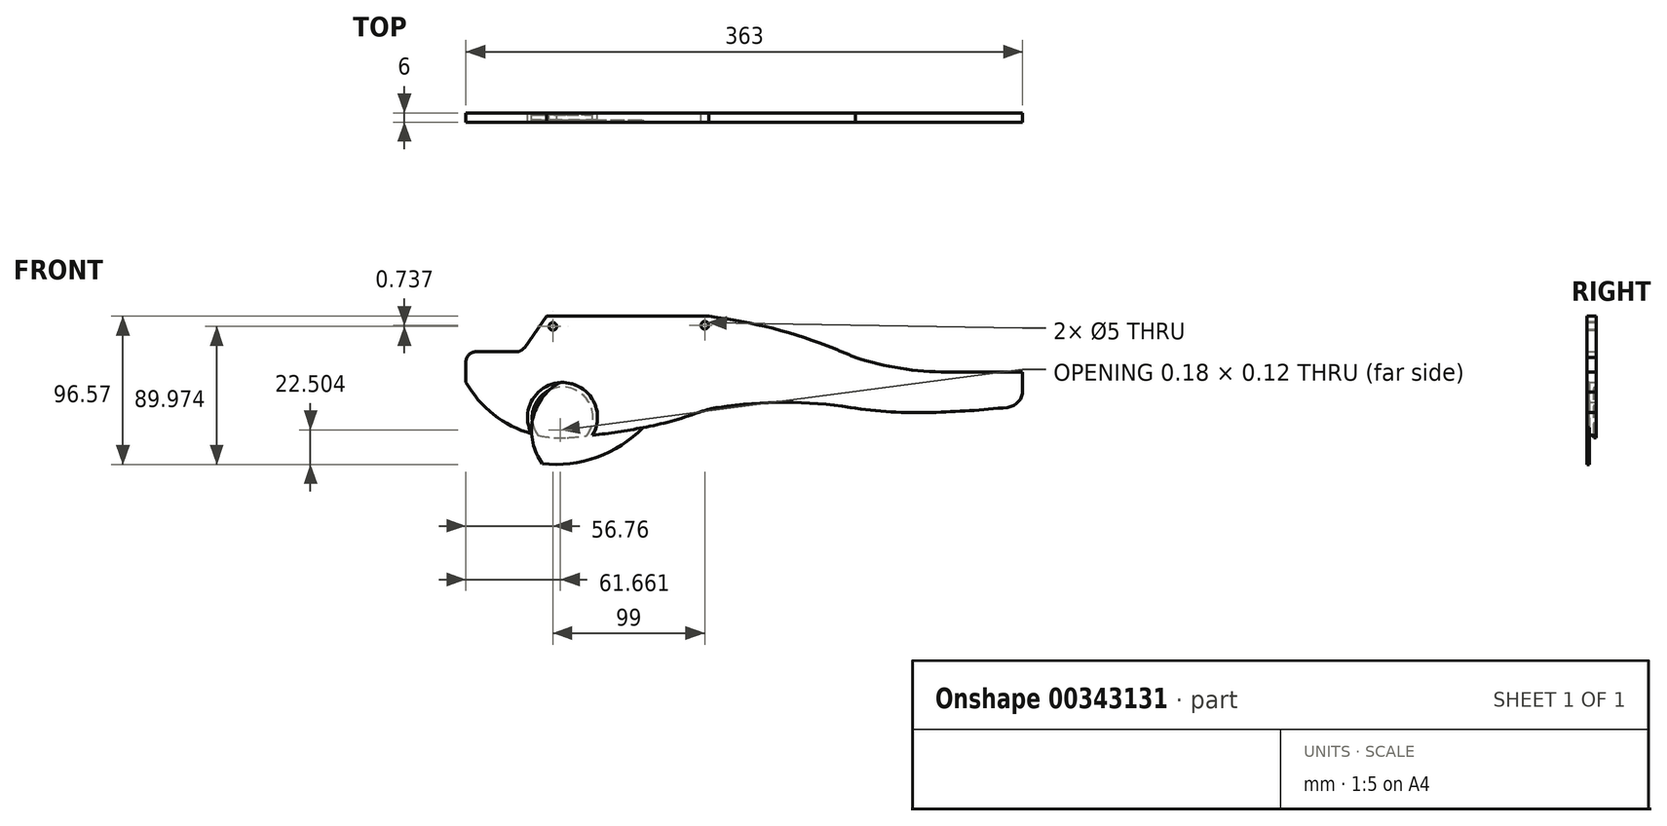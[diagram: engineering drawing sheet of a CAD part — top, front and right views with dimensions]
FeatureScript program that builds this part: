
annotation { "Feature Type Name" : "Feature", "Feature Type Description" : "" }
export const myFeature = defineFeature(function(context is Context, id is Id, definition is map)
    precondition{}
    {
        {
            var Q0;
            Q0=qCreatedBy(makeId("Front.planeOp"),FACE);
            var sketch = newSketch(context, id + "F0", { "sketchPlane" : qUnion([Q0])});
            skLineSegment(sketch, "E0", {"start": v(-42.98, -94.11) * mm, "end": v(-42.93, -88.83) * mm});
            skLineSegment(sketch, "E1", {"start": v(-26.54, -87.6) * mm, "end": v(-25.94, -92.84) * mm});
            skLineSegment(sketch, "E2", {"start": v(-57.63, -92.47) * mm, "end": v(-56.84, -87.23) * mm});
            skLineSegment(sketch, "E3", {"start": v(-60.27, -85.91) * mm, "end": v(-60.27, -101.9) * mm});
            skLineSegment(sketch, "E4", {"start": v(0.29, -136.52) * mm, "end": v(0.29, -27.62) * mm});
            skArc(sketch, "E5", {"start": v(15.17, -136.52) * mm, "mid": v(16.66, -98.58) * mm, "end": v(17.15, -60.62) * mm});
            skLineSegment(sketch, "E6", {"start": v(-95.1, -89.53) * mm, "end": v(-95.1, -113.28) * mm});
            skLineSegment(sketch, "E7", {"start": v(-82.32, -86.89) * mm, "end": v(-82.32, -118.56) * mm});
            skArc(sketch, "E8", {"start": v(-88.17, -97.12) * mm, "mid": v(-95.1, -90.19) * mm, "end": v(-102.03, -97.12) * mm});
            skLineSegment(sketch, "E9", {"start": v(-265.33, -143.12) * mm, "end": v(-265.33, 144.31) * mm});
            skLineSegment(sketch, "E10", {"start": v(173.57, -106.96) * mm, "end": v(173.57, -67.22) * mm});
            skLineSegment(sketch, "E11", {"start": v(181.5, -27.62) * mm, "end": v(181.5, -120.02) * mm});
            skLineSegment(sketch, "E12", {"start": v(-9.14, -134.54) * mm, "end": v(-9.14, -29.6) * mm});
            skLineSegment(sketch, "E13", {"start": v(-256.42, -27.62) * mm, "end": v(-256.42, -136.52) * mm});
            skLineSegment(sketch, "E14", {"start": v(-254.44, -27.62) * mm, "end": v(-254.44, -136.52) * mm});
            skLineSegment(sketch, "E15", {"start": v(9.56, -27.62) * mm, "end": v(9.56, -136.52) * mm});
            skLineSegment(sketch, "E16", {"start": v(7.58, -27.62) * mm, "end": v(7.58, -136.52) * mm});
            skLineSegment(sketch, "E17", {"start": v(-123.43, -141.8) * mm, "end": v(-123.43, -22.34) * mm});
            skCircle(sketch, "E18", {"center": v(64.91, -93.78) * mm, "radius": 4.62 * mm});
            skLineSegment(sketch, "E19", {"start": v(-115.5, -136.52) * mm, "end": v(-115.5, -27.62) * mm});
            skLineSegment(sketch, "E20", {"start": v(-113.53, -27.62) * mm, "end": v(-113.53, -136.52) * mm});
            skLineSegment(sketch, "E21", {"start": v(-131.35, -136.52) * mm, "end": v(-131.35, -27.62) * mm});
            skLineSegment(sketch, "E22", {"start": v(-133.33, -27.62) * mm, "end": v(-133.33, -136.52) * mm});
            skLineSegment(sketch, "E23", {"start": v(8.57, -27.62) * mm, "end": v(8.57, -136.52) * mm});
            skLineSegment(sketch, "E24", {"start": v(-255.43, -136.52) * mm, "end": v(-255.43, -27.62) * mm});
            skLineSegment(sketch, "E25", {"start": v(-141.07, -96.5) * mm, "end": v(-141.07, -91.3) * mm});
            skLineSegment(sketch, "E26", {"start": v(-246.67, -96.5) * mm, "end": v(-246.67, -91.3) * mm});
            skLineSegment(sketch, "E27", {"start": v(15.17, -27.62) * mm, "end": v(15.17, -136.52) * mm});
            skLineSegment(sketch, "E28", {"start": v(282.47, 144.31) * mm, "end": v(282.47, -143.12) * mm});
            skLineSegment(sketch, "E29", {"start": v(-47.86, -100.58) * mm, "end": v(-62.91, -100.58) * mm});
            skLineSegment(sketch, "E30", {"start": v(-255.43, -134.54) * mm, "end": v(8.57, -134.54) * mm});
            skLineSegment(sketch, "E31", {"start": v(-255.43, -136.52) * mm, "end": v(8.57, -136.52) * mm});
            skLineSegment(sketch, "E32", {"start": v(-265.33, -143.12) * mm, "end": v(282.47, -143.12) * mm});
            skCircle(sketch, "E33", {"center": v(-165.87, -104.46) * mm, "radius": 4.62 * mm});
            skLineSegment(sketch, "E34", {"start": v(-246.67, -97.09) * mm, "end": v(-141.07, -97.09) * mm});
            skLineSegment(sketch, "E35", {"start": v(-141.07, -112.93) * mm, "end": v(-246.67, -112.93) * mm});
            skLineSegment(sketch, "E36", {"start": v(-242, -92.47) * mm, "end": v(-141.07, -92.47) * mm});
            skLineSegment(sketch, "E37", {"start": v(-256.42, -136.52) * mm, "end": v(-255.43, -136.52) * mm});
            skLineSegment(sketch, "E38", {"start": v(-246.67, -112.93) * mm, "end": v(-246.67, -97.09) * mm});
            skLineSegment(sketch, "E39", {"start": v(-236.7, -112.93) * mm, "end": v(-240.57, -112.93) * mm});
            skLineSegment(sketch, "E40", {"start": v(-239.4, -108.26) * mm, "end": v(-239.4, -101.75) * mm});
            skLineSegment(sketch, "E41", {"start": v(-236.7, -97.09) * mm, "end": v(-240.57, -97.09) * mm});
            skLineSegment(sketch, "E42", {"start": v(-143.23, -133.22) * mm, "end": v(-103.63, -133.22) * mm});
            skLineSegment(sketch, "E43", {"start": v(-143.23, -136.52) * mm, "end": v(-143.23, -133.22) * mm});
            skLineSegment(sketch, "E44", {"start": v(-130.03, -143.12) * mm, "end": v(-130.03, -146.42) * mm});
            skLineSegment(sketch, "E45", {"start": v(-141.07, -112.93) * mm, "end": v(-141.07, -97.09) * mm});
            skLineSegment(sketch, "E46", {"start": v(-148.76, -103.08) * mm, "end": v(-156.68, -103.08) * mm});
            skLineSegment(sketch, "E47", {"start": v(-156.68, -103.08) * mm, "end": v(-154.52, -102.08) * mm});
            skLineSegment(sketch, "E48", {"start": v(-148.76, -103.08) * mm, "end": v(-150.91, -104.08) * mm});
            skLineSegment(sketch, "E49", {"start": v(-103.63, -133.22) * mm, "end": v(-103.63, -136.52) * mm});
            skLineSegment(sketch, "E50", {"start": v(-79.02, -103.38) * mm, "end": v(-85.62, -103.38) * mm});
            skLineSegment(sketch, "E51", {"start": v(-79.02, -113.28) * mm, "end": v(-85.62, -113.28) * mm});
            skArc(sketch, "E52", {"start": v(-91.47, -113.28) * mm, "mid": v(-89, -105.37) * mm, "end": v(-88.17, -97.12) * mm});
            skArc(sketch, "E53", {"start": v(-102.03, -97.12) * mm, "mid": v(-101.2, -105.37) * mm, "end": v(-98.73, -113.28) * mm});
            skLineSegment(sketch, "E54", {"start": v(-98.07, -103.38) * mm, "end": v(-98.07, -113.28) * mm});
            skLineSegment(sketch, "E55", {"start": v(-92.13, -103.38) * mm, "end": v(-92.13, -113.28) * mm});
            skLineSegment(sketch, "E56", {"start": v(-98.07, -113.28) * mm, "end": v(-98.73, -113.28) * mm});
            skLineSegment(sketch, "E57", {"start": v(-86.85, -118.56) * mm, "end": v(-103.35, -118.56) * mm});
            skLineSegment(sketch, "E58", {"start": v(-92.13, -113.28) * mm, "end": v(-91.47, -113.28) * mm});
            skLineSegment(sketch, "E59", {"start": v(-98.07, -115.26) * mm, "end": v(-98.07, -121.86) * mm});
            skLineSegment(sketch, "E60", {"start": v(-92.13, -115.26) * mm, "end": v(-92.13, -121.86) * mm});
            skLineSegment(sketch, "E61", {"start": v(-99.37, -94.25) * mm, "end": v(-97.97, -92.85) * mm});
            skCircle(sketch, "E62", {"center": v(-98.67, -93.55) * mm, "radius": 0.66 * mm});
            skLineSegment(sketch, "E63", {"start": v(-99.37, -92.85) * mm, "end": v(-97.97, -94.25) * mm});
            skLineSegment(sketch, "E64", {"start": v(-99.37, -99.99) * mm, "end": v(-97.97, -101.39) * mm});
            skCircle(sketch, "E65", {"center": v(-98.67, -100.69) * mm, "radius": 0.66 * mm});
            skLineSegment(sketch, "E66", {"start": v(-99.37, -101.39) * mm, "end": v(-97.97, -99.99) * mm});
            skLineSegment(sketch, "E67", {"start": v(-102.69, -97.12) * mm, "end": v(-87.5, -97.12) * mm});
            skLineSegment(sketch, "E68", {"start": v(-92.23, -92.85) * mm, "end": v(-90.83, -94.25) * mm});
            skCircle(sketch, "E69", {"center": v(-91.53, -93.55) * mm, "radius": 0.66 * mm});
            skLineSegment(sketch, "E70", {"start": v(-92.23, -94.25) * mm, "end": v(-90.83, -92.85) * mm});
            skLineSegment(sketch, "E71", {"start": v(-92.13, -103.38) * mm, "end": v(-98.07, -103.38) * mm});
            skCircle(sketch, "E72", {"center": v(-91.53, -100.69) * mm, "radius": 0.66 * mm});
            skLineSegment(sketch, "E73", {"start": v(-92.23, -101.39) * mm, "end": v(-90.83, -99.99) * mm});
            skLineSegment(sketch, "E74", {"start": v(-92.23, -99.99) * mm, "end": v(-90.83, -101.39) * mm});
            skCircle(sketch, "E75", {"center": v(-95.1, -97.12) * mm, "radius": 1.98 * mm});
            skCircle(sketch, "E76", {"center": v(-73.58, -113.75) * mm, "radius": 4.62 * mm});
            skLineSegment(sketch, "E77", {"start": v(15.17, -136.52) * mm, "end": v(162.34, -120.02) * mm});
            skArc(sketch, "E78", {"start": v(-57.63, -92.47) * mm, "mid": v(-41.88, -100.58) * mm, "end": v(-25.94, -92.84) * mm});
            skArc(sketch, "E79", {"start": v(-47.27, -93.95) * mm, "mid": v(-45.12, -94.06) * mm, "end": v(-42.98, -94.11) * mm});
            skArc(sketch, "E80", {"start": v(-46.25, -100.04) * mm, "mid": v(-44.67, -99.16) * mm, "end": v(-45.46, -97.53) * mm});
            skArc(sketch, "E81", {"start": v(-47.25, -93.95) * mm, "mid": v(-48.63, -94.95) * mm, "end": v(-47.86, -96.48) * mm});
            skLineSegment(sketch, "E82", {"start": v(-47.86, -96.48) * mm, "end": v(-45.42, -97.55) * mm});
            skLineSegment(sketch, "E83", {"start": v(8.57, -143.12) * mm, "end": v(8.57, -146.42) * mm});
            skLineSegment(sketch, "E84", {"start": v(9.56, -136.52) * mm, "end": v(8.57, -136.52) * mm});
            skLineSegment(sketch, "E85", {"start": v(72.28, -137.45) * mm, "end": v(138.28, -137.45) * mm});
            skLineSegment(sketch, "E86", {"start": v(72.28, -138.77) * mm, "end": v(138.28, -138.77) * mm});
            skLineSegment(sketch, "E87", {"start": v(72.28, -138.11) * mm, "end": v(138.28, -138.11) * mm});
            skLineSegment(sketch, "E88", {"start": v(72.28, -137.45) * mm, "end": v(72.28, -135.8) * mm});
            skLineSegment(sketch, "E89", {"start": v(72.28, -138.77) * mm, "end": v(72.28, -137.45) * mm});
            skLineSegment(sketch, "E90", {"start": v(75.58, -138.77) * mm, "end": v(75.58, -137.45) * mm});
            skLineSegment(sketch, "E91", {"start": v(74.92, -138.77) * mm, "end": v(74.92, -137.45) * mm});
            skLineSegment(sketch, "E92", {"start": v(74.26, -138.77) * mm, "end": v(74.26, -137.45) * mm});
            skLineSegment(sketch, "E93", {"start": v(73.6, -138.77) * mm, "end": v(73.6, -137.45) * mm});
            skLineSegment(sketch, "E94", {"start": v(72.94, -138.77) * mm, "end": v(72.94, -137.45) * mm});
            skLineSegment(sketch, "E95", {"start": v(78.88, -138.77) * mm, "end": v(78.88, -135.8) * mm});
            skLineSegment(sketch, "E96", {"start": v(78.22, -138.77) * mm, "end": v(78.22, -137.45) * mm});
            skLineSegment(sketch, "E97", {"start": v(85.48, -138.77) * mm, "end": v(85.48, -135.8) * mm});
            skLineSegment(sketch, "E98", {"start": v(77.56, -138.77) * mm, "end": v(77.56, -137.45) * mm});
            skLineSegment(sketch, "E99", {"start": v(76.9, -138.77) * mm, "end": v(76.9, -137.45) * mm});
            skLineSegment(sketch, "E100", {"start": v(76.24, -138.77) * mm, "end": v(76.24, -137.45) * mm});
            skLineSegment(sketch, "E101", {"start": v(98.68, -138.77) * mm, "end": v(98.68, -135.8) * mm});
            skLineSegment(sketch, "E102", {"start": v(92.08, -138.77) * mm, "end": v(92.08, -135.8) * mm});
            skLineSegment(sketch, "E103", {"start": v(61.37, -106.33) * mm, "end": v(63.52, -105.33) * mm});
            skLineSegment(sketch, "E104", {"start": v(69.29, -106.33) * mm, "end": v(61.37, -106.33) * mm});
            skLineSegment(sketch, "E105", {"start": v(69.29, -106.33) * mm, "end": v(67.13, -107.34) * mm});
            skLineSegment(sketch, "E106", {"start": v(111.88, -138.77) * mm, "end": v(111.88, -135.8) * mm});
            skLineSegment(sketch, "E107", {"start": v(105.28, -138.77) * mm, "end": v(105.28, -135.8) * mm});
            skLineSegment(sketch, "E108", {"start": v(118.48, -138.77) * mm, "end": v(118.48, -135.8) * mm});
            skLineSegment(sketch, "E109", {"start": v(125.08, -138.77) * mm, "end": v(125.08, -135.8) * mm});
            skLineSegment(sketch, "E110", {"start": v(147.17, -143.12) * mm, "end": v(147.17, -146.42) * mm});
            skLineSegment(sketch, "E111", {"start": v(138.28, -138.77) * mm, "end": v(138.28, -135.8) * mm});
            skLineSegment(sketch, "E112", {"start": v(131.68, -138.77) * mm, "end": v(131.68, -135.8) * mm});
            skLineSegment(sketch, "E113", {"start": v(160.37, -106.96) * mm, "end": v(169.7, -116.3) * mm});
            skArc(sketch, "E114", {"start": v(162.34, -120.02) * mm, "mid": v(170.38, -115.57) * mm, "end": v(173.57, -106.96) * mm});
            skLineSegment(sketch, "E115", {"start": v(174.9, -120.02) * mm, "end": v(181.5, -120.02) * mm});
            skLineSegment(sketch, "E116", {"start": v(160.37, -105.31) * mm, "end": v(160.37, -108.61) * mm});
            skLineSegment(sketch, "E117", {"start": v(162.02, -106.96) * mm, "end": v(158.72, -106.96) * mm});
            skLineSegment(sketch, "E118", {"start": v(-24.62, -84.06) * mm, "end": v(-58.95, -84.06) * mm});
            skLineSegment(sketch, "E119", {"start": v(-57.63, -87.23) * mm, "end": v(-62.91, -87.23) * mm});
            skLineSegment(sketch, "E120", {"start": v(124.6, 13.25) * mm, "end": v(-257.96, 13.25) * mm});
            skLineSegment(sketch, "E121", {"start": v(-54.8, 33.74) * mm, "end": v(-61.25, 33.74) * mm});
            skLineSegment(sketch, "E122", {"start": v(-54.8, 43.64) * mm, "end": v(-61.25, 43.64) * mm});
            skLineSegment(sketch, "E123", {"start": v(69.74, 85.08) * mm, "end": v(-206.13, 85.08) * mm});
            skLineSegment(sketch, "E124", {"start": v(-240.46, 57.71) * mm, "end": v(-39.87, 57.71) * mm});
            skLineSegment(sketch, "E125", {"start": v(-255.43, -29.6) * mm, "end": v(8.57, -29.6) * mm});
            skLineSegment(sketch, "E126", {"start": v(-255.43, -27.62) * mm, "end": v(8.57, -27.62) * mm});
            skArc(sketch, "E127", {"start": v(0.09, 100.16) * mm, "mid": v(-40.3, 113.45) * mm, "end": v(-82.06, 121.38) * mm});
            skLineSegment(sketch, "E128", {"start": v(-82.06, 16.22) * mm, "end": v(122.54, 16.22) * mm});
            skLineSegment(sketch, "E129", {"start": v(-82.06, 12.26) * mm, "end": v(122.54, 12.26) * mm});
            skLineSegment(sketch, "E130", {"start": v(-82.06, 10.28) * mm, "end": v(122.54, 10.28) * mm});
            skLineSegment(sketch, "E131", {"start": v(-67.32, 121.38) * mm, "end": v(11.5, 121.38) * mm});
            skLineSegment(sketch, "E132", {"start": v(122.54, 14.24) * mm, "end": v(-82.06, 14.24) * mm});
            skArc(sketch, "E133", {"start": v(10.34, 61.98) * mm, "mid": v(-32.56, 65.28) * mm, "end": v(-75.46, 61.98) * mm});
            skLineSegment(sketch, "E134", {"start": v(-265.33, 144.31) * mm, "end": v(282.47, 144.31) * mm});
            skArc(sketch, "E135", {"start": v(-178.9, 47.37) * mm, "mid": v(-178.8, 47.37) * mm, "end": v(-178.7, 47.37) * mm});
            skArc(sketch, "E136", {"start": v(-171.6, 95.7) * mm, "mid": v(-190.86, 66.6) * mm, "end": v(-165.14, 43) * mm});
            skArc(sketch, "E137", {"start": v(-240.46, 78.48) * mm, "mid": v(-223.34, 58.17) * mm, "end": v(-199.98, 45.5) * mm});
            skLineSegment(sketch, "E138", {"start": v(-240.46, 76.5) * mm, "end": v(-240.46, 31.72) * mm});
            skArc(sketch, "E139", {"start": v(-174.46, 42.18) * mm, "mid": v(-149.62, 44.8) * mm, "end": v(-124.96, 48.78) * mm});
            skArc(sketch, "E140", {"start": v(-193.4, 43.74) * mm, "mid": v(-177.66, 35.62) * mm, "end": v(-161.72, 43.36) * mm});
            skLineSegment(sketch, "E141", {"start": v(-176, -4.6) * mm, "end": v(-157.01, -4.6) * mm});
            skLineSegment(sketch, "E142", {"start": v(-161.03, 31.18) * mm, "end": v(-167.86, 22.82) * mm});
            skLineSegment(sketch, "E143", {"start": v(-174.46, 9.62) * mm, "end": v(-161.26, 9.62) * mm});
            skLineSegment(sketch, "E144", {"start": v(-174.46, 22.82) * mm, "end": v(-161.26, 22.82) * mm});
            skLineSegment(sketch, "E145", {"start": v(-167.86, 6.98) * mm, "end": v(-161.26, 6.98) * mm});
            skLineSegment(sketch, "E146", {"start": v(-166.54, 4.34) * mm, "end": v(-162.58, 4.34) * mm});
            skArc(sketch, "E147", {"start": v(-141.07, -66.86) * mm, "mid": v(-177.15, -60.34) * mm, "end": v(-213.67, -56.96) * mm});
            skLineSegment(sketch, "E148", {"start": v(-246.67, -66.86) * mm, "end": v(-141.07, -66.86) * mm});
            skArc(sketch, "E149", {"start": v(-140.63, -64.93) * mm, "mid": v(-176.88, -58.38) * mm, "end": v(-213.57, -54.98) * mm});
            skLineSegment(sketch, "E150", {"start": v(-243.79, -64.88) * mm, "end": v(-150.34, -64.88) * mm});
            skLineSegment(sketch, "E151", {"start": v(-174.46, 10.28) * mm, "end": v(-161.26, 10.28) * mm});
            skLineSegment(sketch, "E152", {"start": v(-174.46, 12.26) * mm, "end": v(-161.26, 12.26) * mm});
            skLineSegment(sketch, "E153", {"start": v(-174.46, 16.22) * mm, "end": v(-161.26, 16.22) * mm});
            skLineSegment(sketch, "E154", {"start": v(-161.26, 14.24) * mm, "end": v(-174.46, 14.24) * mm});
            skLineSegment(sketch, "E155", {"start": v(-255.43, -25.64) * mm, "end": v(-255.43, -9.14) * mm});
            skArc(sketch, "E156", {"start": v(-213.67, -56.96) * mm, "mid": v(-231.03, -59.03) * mm, "end": v(-246.67, -66.86) * mm});
            skArc(sketch, "E157", {"start": v(-213.57, -54.98) * mm, "mid": v(-231.01, -56.96) * mm, "end": v(-246.85, -64.55) * mm});
            skLineSegment(sketch, "E158", {"start": v(-244.2, -54.23) * mm, "end": v(-246.94, -65.4) * mm});
            skLineSegment(sketch, "E159", {"start": v(-246.33, -64.18) * mm, "end": v(-245.17, -65.79) * mm});
            skArc(sketch, "E160", {"start": v(-246.85, -64.55) * mm, "mid": v(-247.42, -65.75) * mm, "end": v(-246.67, -66.86) * mm});
            skLineSegment(sketch, "E161", {"start": v(-255.43, -27.62) * mm, "end": v(-256.42, -27.62) * mm});
            skLineSegment(sketch, "E162", {"start": v(-255.43, -27.62) * mm, "end": v(-254.1, -27.62) * mm});
            skLineSegment(sketch, "E163", {"start": v(-244.2, -54.23) * mm, "end": v(-238.71, -54.23) * mm});
            skLineSegment(sketch, "E164", {"start": v(-186.91, -52.29) * mm, "end": v(-188.29, -57.87) * mm});
            skLineSegment(sketch, "E165", {"start": v(-198.1, -66.02) * mm, "end": v(-186.91, -52.29) * mm});
            skLineSegment(sketch, "E166", {"start": v(-186.91, -52.29) * mm, "end": v(-170.37, -52.29) * mm});
            skLineSegment(sketch, "E167", {"start": v(-240.87, 21.06) * mm, "end": v(-194.44, 21.06) * mm});
            skLineSegment(sketch, "E168", {"start": v(-233.12, 10.28) * mm, "end": v(-187.66, 10.28) * mm});
            skLineSegment(sketch, "E169", {"start": v(-233.01, 16.22) * mm, "end": v(-187.66, 16.22) * mm});
            skLineSegment(sketch, "E170", {"start": v(-233.08, 12.26) * mm, "end": v(-187.66, 12.26) * mm});
            skLineSegment(sketch, "E171", {"start": v(-187.66, 14.24) * mm, "end": v(-233.05, 14.24) * mm});
            skLineSegment(sketch, "E172", {"start": v(-253.18, 12.9) * mm, "end": v(-253.15, 14.28) * mm});
            skLineSegment(sketch, "E173", {"start": v(-251.24, 12.85) * mm, "end": v(-251.21, 14.24) * mm});
            skLineSegment(sketch, "E174", {"start": v(-257.96, 13.66) * mm, "end": v(-219.59, 13) * mm});
            skLineSegment(sketch, "E175", {"start": v(-233.94, 19.85) * mm, "end": v(-234.17, 6.65) * mm});
            skLineSegment(sketch, "E176", {"start": v(-232.95, 19.83) * mm, "end": v(-233.18, 6.63) * mm});
            skLineSegment(sketch, "E177", {"start": v(-233.95, 19.19) * mm, "end": v(-234.16, 7.3) * mm});
            skLineSegment(sketch, "E178", {"start": v(-235.68, 7.33) * mm, "end": v(-235.47, 19.21) * mm});
            skLineSegment(sketch, "E179", {"start": v(-242.06, 8.67) * mm, "end": v(-241.9, 18.1) * mm});
            skLineSegment(sketch, "E180", {"start": v(-246.94, 8.75) * mm, "end": v(-246.78, 18.19) * mm});
            skLineSegment(sketch, "E181", {"start": v(-251.27, 10.77) * mm, "end": v(-249.63, 10.75) * mm});
            skLineSegment(sketch, "E182", {"start": v(-251.18, 16.32) * mm, "end": v(-249.53, 16.29) * mm});
            skLineSegment(sketch, "E183", {"start": v(-251.27, 10.77) * mm, "end": v(-251.18, 16.32) * mm});
            skLineSegment(sketch, "E184", {"start": v(-252.75, 12.32) * mm, "end": v(-252.7, 14.83) * mm});
            skLineSegment(sketch, "E185", {"start": v(-252.7, 14.83) * mm, "end": v(-251.2, 14.8) * mm});
            skLineSegment(sketch, "E186", {"start": v(-252.75, 12.32) * mm, "end": v(-251.25, 12.3) * mm});
            skLineSegment(sketch, "E187", {"start": v(-238.83, 10.03) * mm, "end": v(-238.72, 16.63) * mm});
            skLineSegment(sketch, "E188", {"start": v(-241.94, 15.36) * mm, "end": v(-238.74, 15.3) * mm});
            skLineSegment(sketch, "E189", {"start": v(-249.63, 10.75) * mm, "end": v(-249.53, 16.29) * mm});
            skLineSegment(sketch, "E190", {"start": v(-238.72, 16.63) * mm, "end": v(-235.52, 16.57) * mm});
            skLineSegment(sketch, "E191", {"start": v(-246.78, 18.19) * mm, "end": v(-241.9, 18.1) * mm});
            skLineSegment(sketch, "E192", {"start": v(-235.47, 19.21) * mm, "end": v(-233.95, 19.19) * mm});
            skLineSegment(sketch, "E193", {"start": v(-238.83, 10.03) * mm, "end": v(-235.63, 9.97) * mm});
            skLineSegment(sketch, "E194", {"start": v(-247.87, 12.5) * mm, "end": v(-247.83, 14.48) * mm});
            skLineSegment(sketch, "E195", {"start": v(-248.52, 12.5) * mm, "end": v(-248.5, 14.49) * mm});
            skLineSegment(sketch, "E196", {"start": v(-247.83, 14.48) * mm, "end": v(-246.84, 14.46) * mm});
            skLineSegment(sketch, "E197", {"start": v(-249.55, 14.77) * mm, "end": v(-248.5, 14.49) * mm});
            skLineSegment(sketch, "E198", {"start": v(-248.52, 13) * mm, "end": v(-247.86, 13) * mm});
            skLineSegment(sketch, "E199", {"start": v(-248.5, 14) * mm, "end": v(-247.84, 13.98) * mm});
            skLineSegment(sketch, "E200", {"start": v(-242, 11.4) * mm, "end": v(-238.8, 11.35) * mm});
            skLineSegment(sketch, "E201", {"start": v(-247.87, 12.5) * mm, "end": v(-246.88, 12.48) * mm});
            skLineSegment(sketch, "E202", {"start": v(-249.6, 12.26) * mm, "end": v(-248.52, 12.5) * mm});
            skLineSegment(sketch, "E203", {"start": v(-246.94, 8.75) * mm, "end": v(-242.06, 8.67) * mm});
            skLineSegment(sketch, "E204", {"start": v(-235.68, 7.33) * mm, "end": v(-234.16, 7.3) * mm});
            skLineSegment(sketch, "E205", {"start": v(-240.46, 16.22) * mm, "end": v(-240.46, 10.28) * mm});
            skLineSegment(sketch, "E206", {"start": v(-251.6, -1.17) * mm, "end": v(-251.24, 12.85) * mm});
            skLineSegment(sketch, "E207", {"start": v(-253.18, 12.9) * mm, "end": v(-253.19, -1.87) * mm});
            skLineSegment(sketch, "E208", {"start": v(-234.17, 6.65) * mm, "end": v(-233.18, 6.63) * mm});
            skLineSegment(sketch, "E209", {"start": v(-240.46, 10.28) * mm, "end": v(-234.1, 10.28) * mm});
            skLineSegment(sketch, "E210", {"start": v(-251.05, 33.32) * mm, "end": v(-251.22, 14.25) * mm});
            skLineSegment(sketch, "E211", {"start": v(-253.15, 14.28) * mm, "end": v(-252.49, 33.79) * mm});
            skLineSegment(sketch, "E212", {"start": v(-240.87, 21.06) * mm, "end": v(-243.25, 18.15) * mm});
            skLineSegment(sketch, "E213", {"start": v(-233.94, 19.85) * mm, "end": v(-232.95, 19.83) * mm});
            skLineSegment(sketch, "E214", {"start": v(-240.46, 16.22) * mm, "end": v(-234, 16.22) * mm});
            skLineSegment(sketch, "E215", {"start": v(-179.64, 16.76) * mm, "end": v(-179.64, 8.84) * mm});
            skLineSegment(sketch, "E216", {"start": v(-187.66, 3.35) * mm, "end": v(-187.66, 23.15) * mm});
            skLineSegment(sketch, "E217", {"start": v(-174.46, 23.15) * mm, "end": v(-174.46, 3.35) * mm});
            skLineSegment(sketch, "E218", {"start": v(-185.02, 3.35) * mm, "end": v(-185.02, 23.15) * mm});
            skLineSegment(sketch, "E219", {"start": v(-182.38, 23.15) * mm, "end": v(-182.38, 3.35) * mm});
            skLineSegment(sketch, "E220", {"start": v(-209.11, 14.24) * mm, "end": v(-209.11, 12.26) * mm});
            skLineSegment(sketch, "E221", {"start": v(-212.41, 14.24) * mm, "end": v(-212.41, 12.26) * mm});
            skCircle(sketch, "E222", {"center": v(-193.46, 4.9) * mm, "radius": 4.62 * mm});
            skLineSegment(sketch, "E223", {"start": v(-176, -4.6) * mm, "end": v(-183.7, 1.7) * mm});
            skLineSegment(sketch, "E224", {"start": v(-174.46, 3.35) * mm, "end": v(-187.66, 3.35) * mm});
            skLineSegment(sketch, "E225", {"start": v(-182.38, 3.35) * mm, "end": v(-182.38, 1.7) * mm});
            skLineSegment(sketch, "E226", {"start": v(-185.02, 3.35) * mm, "end": v(-185.02, 1.7) * mm});
            skLineSegment(sketch, "E227", {"start": v(-182.38, 1.7) * mm, "end": v(-185.02, 1.7) * mm});
            skLineSegment(sketch, "E228", {"start": v(-179.64, 8.84) * mm, "end": v(-180.64, 11) * mm});
            skLineSegment(sketch, "E229", {"start": v(-167.86, 6.98) * mm, "end": v(-167.86, 9.62) * mm});
            skLineSegment(sketch, "E230", {"start": v(-167.86, 8.3) * mm, "end": v(-169.84, 8.3) * mm});
            skLineSegment(sketch, "E231", {"start": v(-169.84, 8.3) * mm, "end": v(-169.84, 9.62) * mm});
            skLineSegment(sketch, "E232", {"start": v(-166.54, 4.34) * mm, "end": v(-166.54, 6.98) * mm});
            skArc(sketch, "E233", {"start": v(-199.98, 45.5) * mm, "mid": v(-187.37, 42.69) * mm, "end": v(-174.46, 42.18) * mm});
            skLineSegment(sketch, "E234", {"start": v(-179.64, 16.76) * mm, "end": v(-178.64, 14.61) * mm});
            skLineSegment(sketch, "E235", {"start": v(-187.66, 23.15) * mm, "end": v(-174.46, 23.15) * mm});
            skLineSegment(sketch, "E236", {"start": v(-182.38, 24.8) * mm, "end": v(-182.38, 23.15) * mm});
            skLineSegment(sketch, "E237", {"start": v(-185.02, 24.8) * mm, "end": v(-185.02, 23.15) * mm});
            skLineSegment(sketch, "E238", {"start": v(-185.02, 24.8) * mm, "end": v(-182.38, 24.8) * mm});
            skArc(sketch, "E239", {"start": v(-182.02, 36.16) * mm, "mid": v(-182, 36.16) * mm, "end": v(-182, 36.16) * mm});
            skLineSegment(sketch, "E240", {"start": v(-181.23, 38.67) * mm, "end": v(-181.2, 38.66) * mm});
            skArc(sketch, "E241", {"start": v(-183.02, 42.26) * mm, "mid": v(-183.03, 42.26) * mm, "end": v(-183.04, 42.26) * mm});
            skLineSegment(sketch, "E242", {"start": v(-178.7, 47.25) * mm, "end": v(-178.7, 47.37) * mm});
            skCircle(sketch, "E243", {"center": v(-104.66, -18.88) * mm, "radius": 4.62 * mm});
            skLineSegment(sketch, "E244", {"start": v(-97.03, -22.95) * mm, "end": v(-97.03, -18.28) * mm});
            skLineSegment(sketch, "E245", {"start": v(-133.33, -26.3) * mm, "end": v(-133.33, -19.04) * mm});
            skLineSegment(sketch, "E246", {"start": v(-113.53, -26.3) * mm, "end": v(-113.53, -19.04) * mm});
            skLineSegment(sketch, "E247", {"start": v(-138.56, -36.7) * mm, "end": v(-108.3, -36.7) * mm});
            skLineSegment(sketch, "E248", {"start": v(-143.23, -30.92) * mm, "end": v(-103.63, -30.92) * mm});
            skCircle(sketch, "E249", {"center": v(-156.91, -73.53) * mm, "radius": 4.62 * mm});
            skLineSegment(sketch, "E250", {"start": v(-160.11, -70.2) * mm, "end": v(-164.23, -65.92) * mm});
            skLineSegment(sketch, "E251", {"start": v(-140.63, -64.93) * mm, "end": v(-141.07, -66.86) * mm});
            skLineSegment(sketch, "E252", {"start": v(-142.56, -64.5) * mm, "end": v(-143, -66.43) * mm});
            skLineSegment(sketch, "E253", {"start": v(-143.26, -59.23) * mm, "end": v(-141.7, -65.6) * mm});
            skLineSegment(sketch, "E254", {"start": v(-148.95, -59.23) * mm, "end": v(-143.26, -59.23) * mm});
            skLineSegment(sketch, "E255", {"start": v(-143.23, -32.24) * mm, "end": v(-143.23, -38.69) * mm});
            skLineSegment(sketch, "E256", {"start": v(-143.23, -27.62) * mm, "end": v(-143.23, -30.92) * mm});
            skLineSegment(sketch, "E257", {"start": v(-79.02, -90.19) * mm, "end": v(-85.62, -90.19) * mm});
            skLineSegment(sketch, "E258", {"start": v(-85.2, -87.12) * mm, "end": v(-105, -87.12) * mm});
            skLineSegment(sketch, "E259", {"start": v(-101.7, -83.82) * mm, "end": v(-101.7, -90.42) * mm});
            skLineSegment(sketch, "E260", {"start": v(-88.5, -83.8) * mm, "end": v(-88.5, -90.4) * mm});
            skCircle(sketch, "E261", {"center": v(-105.59, -63.06) * mm, "radius": 4.62 * mm});
            skLineSegment(sketch, "E262", {"start": v(-59.28, -59.26) * mm, "end": v(-61.43, -60.27) * mm});
            skLineSegment(sketch, "E263", {"start": v(-67.2, -59.26) * mm, "end": v(-65.04, -58.26) * mm});
            skLineSegment(sketch, "E264", {"start": v(-59.28, -59.26) * mm, "end": v(-67.2, -59.26) * mm});
            skLineSegment(sketch, "E265", {"start": v(-97.03, -35.58) * mm, "end": v(-97.03, -40.25) * mm});
            skLineSegment(sketch, "E266", {"start": v(-102.3, -30.92) * mm, "end": v(-95.86, -30.92) * mm});
            skLineSegment(sketch, "E267", {"start": v(-103.63, -32.24) * mm, "end": v(-103.63, -38.69) * mm});
            skLineSegment(sketch, "E268", {"start": v(-103.63, -30.92) * mm, "end": v(-103.63, -27.62) * mm});
            skLineSegment(sketch, "E269", {"start": v(-97.03, -30.92) * mm, "end": v(-97.03, -27.62) * mm});
            skCircle(sketch, "E270", {"center": v(-63.65, -46.7) * mm, "radius": 4.62 * mm});
            skLineSegment(sketch, "E271", {"start": v(-148.06, 16.22) * mm, "end": v(-95.26, 16.22) * mm});
            skLineSegment(sketch, "E272", {"start": v(-148.06, 12.26) * mm, "end": v(-95.26, 12.26) * mm});
            skLineSegment(sketch, "E273", {"start": v(-148.06, 10.28) * mm, "end": v(-95.26, 10.28) * mm});
            skLineSegment(sketch, "E274", {"start": v(-95.26, 14.24) * mm, "end": v(-148.06, 14.24) * mm});
            skLineSegment(sketch, "E275", {"start": v(-141.47, 19.52) * mm, "end": v(-141.47, 3.68) * mm});
            skLineSegment(sketch, "E276", {"start": v(-161.26, 3.35) * mm, "end": v(-161.26, 23.15) * mm});
            skLineSegment(sketch, "E277", {"start": v(-148.06, 23.15) * mm, "end": v(-148.06, 3.35) * mm});
            skLineSegment(sketch, "E278", {"start": v(-148.06, 3.35) * mm, "end": v(-161.26, 3.35) * mm});
            skLineSegment(sketch, "E279", {"start": v(-162.58, 4.34) * mm, "end": v(-162.58, 6.98) * mm});
            skLineSegment(sketch, "E280", {"start": v(-148.06, 3.68) * mm, "end": v(-141.47, 3.68) * mm});
            skLineSegment(sketch, "E281", {"start": v(-118.2, -21.02) * mm, "end": v(-128.66, -21.02) * mm});
            skLineSegment(sketch, "E282", {"start": v(-161.03, 31.18) * mm, "end": v(-124.29, 31.18) * mm});
            skLineSegment(sketch, "E283", {"start": v(-161.03, 31.18) * mm, "end": v(-144.77, 22.16) * mm});
            skLineSegment(sketch, "E284", {"start": v(-161.26, 23.15) * mm, "end": v(-148.06, 23.15) * mm});
            skLineSegment(sketch, "E285", {"start": v(-156.6, 18.2) * mm, "end": v(-152.73, 18.2) * mm});
            skLineSegment(sketch, "E286", {"start": v(-148.07, 16.88) * mm, "end": v(-138.83, 16.88) * mm});
            skLineSegment(sketch, "E287", {"start": v(-138.83, 16.88) * mm, "end": v(-138.83, 16.22) * mm});
            skLineSegment(sketch, "E288", {"start": v(-148.07, 19.52) * mm, "end": v(-141.47, 19.52) * mm});
            skLineSegment(sketch, "E289", {"start": v(-146.75, 22.16) * mm, "end": v(-146.75, 19.52) * mm});
            skLineSegment(sketch, "E290", {"start": v(-146.75, 22.16) * mm, "end": v(-142.79, 22.16) * mm});
            skLineSegment(sketch, "E291", {"start": v(-142.79, 22.16) * mm, "end": v(-142.79, 19.52) * mm});
            skLineSegment(sketch, "E292", {"start": v(-141.47, 16.22) * mm, "end": v(-138.83, 16.22) * mm});
            skLineSegment(sketch, "E293", {"start": v(-74.93, 1.7) * mm, "end": v(-74.93, 24.8) * mm});
            skLineSegment(sketch, "E294", {"start": v(-95.26, 3.35) * mm, "end": v(-95.26, 23.15) * mm});
            skLineSegment(sketch, "E295", {"start": v(-82.06, 23.15) * mm, "end": v(-82.06, 3.35) * mm});
            skLineSegment(sketch, "E296", {"start": v(-86.02, 3.35) * mm, "end": v(-86.02, 23.15) * mm});
            skLineSegment(sketch, "E297", {"start": v(-83.38, 23.15) * mm, "end": v(-83.38, 3.35) * mm});
            skLineSegment(sketch, "E298", {"start": v(-90, 3.35) * mm, "end": v(-90, 23.15) * mm});
            skLineSegment(sketch, "E299", {"start": v(-83.38, 1.7) * mm, "end": v(-86.02, 1.7) * mm});
            skLineSegment(sketch, "E300", {"start": v(-82.06, 3.35) * mm, "end": v(-95.26, 3.35) * mm});
            skLineSegment(sketch, "E301", {"start": v(-86.02, 3.35) * mm, "end": v(-86.02, 1.7) * mm});
            skLineSegment(sketch, "E302", {"start": v(-81.53, 1.7) * mm, "end": v(-73.6, 1.7) * mm});
            skLineSegment(sketch, "E303", {"start": v(-83.38, 3.35) * mm, "end": v(-83.38, 1.7) * mm});
            skLineSegment(sketch, "E304", {"start": v(-87.23, 27.9) * mm, "end": v(-84.7, 24.8) * mm});
            skLineSegment(sketch, "E305", {"start": v(-86.02, 24.8) * mm, "end": v(-83.38, 24.8) * mm});
            skLineSegment(sketch, "E306", {"start": v(-95.26, 23.15) * mm, "end": v(-82.06, 23.15) * mm});
            skLineSegment(sketch, "E307", {"start": v(-108.32, 27.9) * mm, "end": v(-87.23, 27.9) * mm});
            skLineSegment(sketch, "E308", {"start": v(-86.02, 24.8) * mm, "end": v(-86.02, 23.15) * mm});
            skLineSegment(sketch, "E309", {"start": v(-81.53, 24.8) * mm, "end": v(-73.6, 24.8) * mm});
            skLineSegment(sketch, "E310", {"start": v(-83.38, 24.8) * mm, "end": v(-83.38, 23.15) * mm});
            skLineSegment(sketch, "E311", {"start": v(-60.08, 29.07) * mm, "end": v(-60.08, 24.4) * mm});
            skLineSegment(sketch, "E312", {"start": v(-60.08, 33.74) * mm, "end": v(-60.08, 43.64) * mm});
            skLineSegment(sketch, "E313", {"start": v(-82.06, 121.38) * mm, "end": v(-171.6, 95.7) * mm});
            skArc(sketch, "E314", {"start": v(-204.54, 99.02) * mm, "mid": v(-181.68, 101.24) * mm, "end": v(-170.65, 121.38) * mm});
            skLineSegment(sketch, "E315", {"start": v(-187.66, 121.38) * mm, "end": v(-82.06, 121.38) * mm});
            skLineSegment(sketch, "E316", {"start": v(-240.46, 127.98) * mm, "end": v(-82.06, 127.98) * mm});
            skLineSegment(sketch, "E317", {"start": v(-254.63, 131.16) * mm, "end": v(-251.46, 90.82) * mm});
            skLineSegment(sketch, "E318", {"start": v(-253.4, 90.68) * mm, "end": v(-255.52, 130.84) * mm});
            skFitSpline(sketch, "E319", {"points": [v(-255.52, 130.84) * mm, v(-255.52, 131) * mm, v(-255.52, 131.2) * mm, v(-255.5, 131.46) * mm, v(-255.42, 131.67) * mm, v(-255.21, 131.84) * mm, v(-254.97, 131.9) * mm, v(-254.72, 131.82) * mm, v(-254.66, 131.5) * mm, v(-254.64, 131.28) * mm, v(-254.63, 131.16) * mm]});
            skLineSegment(sketch, "E320", {"start": v(-253.3, 89.3) * mm, "end": v(-249.82, 49.23) * mm});
            skLineSegment(sketch, "E321", {"start": v(-248.89, 49.04) * mm, "end": v(-251.36, 89.43) * mm});
            skFitSpline(sketch, "E322", {"points": [v(-249.82, 49.23) * mm, v(-249.8, 49.08) * mm, v(-249.76, 48.89) * mm, v(-249.71, 48.62) * mm, v(-249.6, 48.43) * mm, v(-249.37, 48.29) * mm, v(-249.12, 48.26) * mm, v(-248.89, 48.37) * mm, v(-248.87, 48.7) * mm, v(-248.88, 48.92) * mm, v(-248.89, 49.04) * mm]});
            skLineSegment(sketch, "E323", {"start": v(-251.46, 90.82) * mm, "end": v(-251.36, 89.44) * mm});
            skLineSegment(sketch, "E324", {"start": v(-253.4, 90.68) * mm, "end": v(-253.3, 89.3) * mm});
            skLineSegment(sketch, "E325", {"start": v(-240.46, 95.64) * mm, "end": v(-240.46, 129.15) * mm});
            skLineSegment(sketch, "E326", {"start": v(-187.66, 120.06) * mm, "end": v(-187.66, 103.72) * mm});
            skLineSegment(sketch, "E327", {"start": v(-176.44, 114.78) * mm, "end": v(-176.44, 121.38) * mm});
            skLineSegment(sketch, "E328", {"start": v(-187.66, 121.38) * mm, "end": v(-202.19, 101.05) * mm});
            skLineSegment(sketch, "E329", {"start": v(-183.7, 118.08) * mm, "end": v(-183.7, 110.16) * mm});
            skLineSegment(sketch, "E330", {"start": v(-216.7, 85.08) * mm, "end": v(-259.06, 85.08) * mm});
            skLineSegment(sketch, "E331", {"start": v(-207.56, 98.28) * mm, "end": v(-233.86, 98.28) * mm});
            skLineSegment(sketch, "E332", {"start": v(-240.46, 91.68) * mm, "end": v(-240.46, 78.48) * mm});
            skLineSegment(sketch, "E333", {"start": v(-242.5, 95.48) * mm, "end": v(-241.85, 86.07) * mm});
            skLineSegment(sketch, "E334", {"start": v(-247.38, 95.14) * mm, "end": v(-246.72, 85.73) * mm});
            skLineSegment(sketch, "E335", {"start": v(-251.6, 92.9) * mm, "end": v(-249.96, 93.01) * mm});
            skLineSegment(sketch, "E336", {"start": v(-251.22, 87.37) * mm, "end": v(-249.57, 87.48) * mm});
            skLineSegment(sketch, "E337", {"start": v(-251.6, 92.9) * mm, "end": v(-251.22, 87.37) * mm});
            skLineSegment(sketch, "E338", {"start": v(-253, 91.28) * mm, "end": v(-252.82, 88.77) * mm});
            skLineSegment(sketch, "E339", {"start": v(-252.82, 88.77) * mm, "end": v(-251.32, 88.88) * mm});
            skLineSegment(sketch, "E340", {"start": v(-253, 91.28) * mm, "end": v(-251.5, 91.38) * mm});
            skLineSegment(sketch, "E341", {"start": v(-242.04, 88.8) * mm, "end": v(-240.46, 88.91) * mm});
            skLineSegment(sketch, "E342", {"start": v(-249.96, 93.01) * mm, "end": v(-249.57, 87.48) * mm});
            skLineSegment(sketch, "E343", {"start": v(-246.72, 85.73) * mm, "end": v(-241.85, 86.07) * mm});
            skLineSegment(sketch, "E344", {"start": v(-248.1, 91.35) * mm, "end": v(-247.97, 89.38) * mm});
            skLineSegment(sketch, "E345", {"start": v(-248.77, 91.3) * mm, "end": v(-248.63, 89.33) * mm});
            skLineSegment(sketch, "E346", {"start": v(-247.97, 89.38) * mm, "end": v(-246.98, 89.45) * mm});
            skLineSegment(sketch, "E347", {"start": v(-249.68, 89) * mm, "end": v(-248.63, 89.33) * mm});
            skLineSegment(sketch, "E348", {"start": v(-248.73, 90.81) * mm, "end": v(-248.07, 90.86) * mm});
            skLineSegment(sketch, "E349", {"start": v(-248.66, 89.83) * mm, "end": v(-248, 89.87) * mm});
            skLineSegment(sketch, "E350", {"start": v(-248.1, 91.35) * mm, "end": v(-247.12, 91.42) * mm});
            skLineSegment(sketch, "E351", {"start": v(-249.85, 91.5) * mm, "end": v(-248.77, 91.3) * mm});
            skLineSegment(sketch, "E352", {"start": v(-247.38, 95.14) * mm, "end": v(-242.5, 95.48) * mm});
            skLineSegment(sketch, "E353", {"start": v(-259.06, 89.6) * mm, "end": v(-220.73, 92.28) * mm});
            skLineSegment(sketch, "E354", {"start": v(-240.46, 98.87) * mm, "end": v(-240.46, 109.35) * mm});
            skArc(sketch, "E355", {"start": v(-233.86, 98.28) * mm, "mid": v(-238.53, 96.35) * mm, "end": v(-240.46, 91.68) * mm});
            skLineSegment(sketch, "E356", {"start": v(-196.15, 109.5) * mm, "end": v(-197, 109.5) * mm});
            skArc(sketch, "E357", {"start": v(-207.56, 98.28) * mm, "mid": v(-204.54, 99.02) * mm, "end": v(-202.19, 101.05) * mm});
            skLineSegment(sketch, "E358", {"start": v(-187.66, 114.86) * mm, "end": v(-187.66, 108.34) * mm});
            skLineSegment(sketch, "E359", {"start": v(-187, 114.78) * mm, "end": v(-183.7, 114.78) * mm});
            skLineSegment(sketch, "E360", {"start": v(-179.03, 109.5) * mm, "end": v(-174.37, 109.5) * mm});
            skLineSegment(sketch, "E361", {"start": v(-183, 104.88) * mm, "end": v(-177.34, 104.88) * mm});
            skLineSegment(sketch, "E362", {"start": v(-179.82, 114.78) * mm, "end": v(-175.27, 114.78) * mm});
            skLineSegment(sketch, "E363", {"start": v(-187.66, 114.2) * mm, "end": v(-187.66, 108.34) * mm});
            skLineSegment(sketch, "E364", {"start": v(-183.7, 114.2) * mm, "end": v(-183.7, 108.34) * mm});
            skLineSegment(sketch, "E365", {"start": v(-176.44, 110.12) * mm, "end": v(-176.44, 105.45) * mm});
            skLineSegment(sketch, "E366", {"start": v(-240.46, 118.67) * mm, "end": v(-240.46, 136.56) * mm});
            skLineSegment(sketch, "E367", {"start": v(-187.66, 122.7) * mm, "end": v(-174.46, 122.7) * mm});
            skLineSegment(sketch, "E368", {"start": v(-187.66, 122.7) * mm, "end": v(-187.66, 121.38) * mm});
            skLineSegment(sketch, "E369", {"start": v(-187.66, 123.26) * mm, "end": v(-187.66, 129.15) * mm});
            skLineSegment(sketch, "E370", {"start": v(-174.46, 121.38) * mm, "end": v(-174.46, 122.7) * mm});
            skLineSegment(sketch, "E371", {"start": v(-176.44, 126.05) * mm, "end": v(-176.44, 130.72) * mm});
            skLineSegment(sketch, "E372", {"start": v(-82.06, 101.14) * mm, "end": v(-82.06, 103.56) * mm});
            skLineSegment(sketch, "E373", {"start": v(-73.6, 129.3) * mm, "end": v(-73.6, 106.86) * mm});
            skLineSegment(sketch, "E374", {"start": v(-141.46, 122.7) * mm, "end": v(-141.46, 121.38) * mm});
            skLineSegment(sketch, "E375", {"start": v(-84.7, 118.08) * mm, "end": v(-84.7, 115.52) * mm});
            skArc(sketch, "E376", {"start": v(-124.96, 48.78) * mm, "mid": v(-106.61, 53.01) * mm, "end": v(-88.66, 58.68) * mm});
            skArc(sketch, "E377", {"start": v(-75.46, 61.98) * mm, "mid": v(-82.14, 60.67) * mm, "end": v(-88.66, 58.68) * mm});
            skLineSegment(sketch, "E378", {"start": v(-88.56, 67.24) * mm, "end": v(-86.41, 68.25) * mm});
            skLineSegment(sketch, "E379", {"start": v(-60.08, 48.3) * mm, "end": v(-60.08, 52.97) * mm});
            skLineSegment(sketch, "E380", {"start": v(-80.64, 67.24) * mm, "end": v(-82.8, 66.24) * mm});
            skLineSegment(sketch, "E381", {"start": v(-88, 114.78) * mm, "end": v(-71.62, 114.78) * mm});
            skLineSegment(sketch, "E382", {"start": v(-77.4, 103.56) * mm, "end": v(-74.14, 103.56) * mm});
            skLineSegment(sketch, "E383", {"start": v(-84.7, 115.52) * mm, "end": v(-84.7, 108.18) * mm});
            skLineSegment(sketch, "E384", {"start": v(-161.26, 122.7) * mm, "end": v(-148.06, 122.7) * mm});
            skLineSegment(sketch, "E385", {"start": v(-161.26, 122.7) * mm, "end": v(-161.26, 121.38) * mm});
            skLineSegment(sketch, "E386", {"start": v(-141.46, 127.37) * mm, "end": v(-141.46, 132.04) * mm});
            skLineSegment(sketch, "E387", {"start": v(-147.48, 122.7) * mm, "end": v(-140.3, 122.7) * mm});
            skLineSegment(sketch, "E388", {"start": v(-148.06, 121.38) * mm, "end": v(-148.06, 122.7) * mm});
            skLineSegment(sketch, "E389", {"start": v(-95.26, 122.7) * mm, "end": v(-82.06, 122.7) * mm});
            skLineSegment(sketch, "E390", {"start": v(-95.26, 122.7) * mm, "end": v(-95.26, 121.38) * mm});
            skLineSegment(sketch, "E391", {"start": v(-82.06, 124.02) * mm, "end": v(-82.06, 129.15) * mm});
            skLineSegment(sketch, "E392", {"start": v(-82.06, 121.38) * mm, "end": v(-82.06, 122.7) * mm});
            skArc(sketch, "E393", {"start": v(173.57, -67.22) * mm, "mid": v(161.98, -39.21) * mm, "end": v(133.97, -27.62) * mm});
            skLineSegment(sketch, "E394", {"start": v(152.94, 68.91) * mm, "end": v(278.34, 68.91) * mm});
            skLineSegment(sketch, "E395", {"start": v(152.94, 81.45) * mm, "end": v(278.34, 81.45) * mm});
            skLineSegment(sketch, "E396", {"start": v(135.74, 27.02) * mm, "end": v(172.93, 15.68) * mm});
            skLineSegment(sketch, "E397", {"start": v(135.05, 24.76) * mm, "end": v(172.93, 13.2) * mm});
            skLineSegment(sketch, "E398", {"start": v(133.97, -67.22) * mm, "end": v(161.98, -39.21) * mm});
            skLineSegment(sketch, "E399", {"start": v(152.94, 68.58) * mm, "end": v(159.54, 52.08) * mm});
            skLineSegment(sketch, "E400", {"start": v(151.46, 94.72) * mm, "end": v(172, 94.72) * mm});
            skLineSegment(sketch, "E401", {"start": v(152.94, 45.48) * mm, "end": v(159.54, 45.48) * mm});
            skLineSegment(sketch, "E402", {"start": v(160.16, 101.32) * mm, "end": v(152.98, 101.32) * mm});
            skLineSegment(sketch, "E403", {"start": v(160.16, 107.92) * mm, "end": v(152.98, 107.92) * mm});
            skLineSegment(sketch, "E404", {"start": v(146.34, 124.68) * mm, "end": v(238.74, 124.68) * mm});
            skLineSegment(sketch, "E405", {"start": v(146.34, 75.18) * mm, "end": v(278.34, 75.18) * mm});
            skLineSegment(sketch, "E406", {"start": v(151, 134.58) * mm, "end": v(273.67, 134.58) * mm});
            skLineSegment(sketch, "E407", {"start": v(151, 127.98) * mm, "end": v(228.84, 127.98) * mm});
            skLineSegment(sketch, "E408", {"start": v(15.17, -83.72) * mm, "end": v(168.9, -83.72) * mm});
            skLineSegment(sketch, "E409", {"start": v(152.94, 60.33) * mm, "end": v(152.94, 37.72) * mm});
            skLineSegment(sketch, "E410", {"start": v(53.24, 46.8) * mm, "end": v(53.24, 48.78) * mm});
            skLineSegment(sketch, "E411", {"start": v(-20.48, 44.22) * mm, "end": v(-20.48, 48.1) * mm});
            skLineSegment(sketch, "E412", {"start": v(-53.48, 35.06) * mm, "end": v(-53.48, 48.1) * mm});
            skLineSegment(sketch, "E413", {"start": v(76.57, -71.6) * mm, "end": v(37.15, -71.6) * mm});
            skLineSegment(sketch, "E414", {"start": v(76.57, -70.28) * mm, "end": v(36.4, -70.28) * mm});
            skLineSegment(sketch, "E415", {"start": v(45.4, -76.76) * mm, "end": v(52.87, -76.76) * mm});
            skLineSegment(sketch, "E416", {"start": v(28, -51.6) * mm, "end": v(60.17, -51.6) * mm});
            skLineSegment(sketch, "E417", {"start": v(15.17, -27.62) * mm, "end": v(133.97, -27.62) * mm});
            skLineSegment(sketch, "E418", {"start": v(-53.48, 33.74) * mm, "end": v(52.12, 33.74) * mm});
            skArc(sketch, "E419", {"start": v(52.12, 33.74) * mm, "mid": v(16.03, 40.25) * mm, "end": v(-20.48, 43.64) * mm});
            skLineSegment(sketch, "E420", {"start": v(8.57, -25.64) * mm, "end": v(8.57, -9.14) * mm});
            skArc(sketch, "E421", {"start": v(-39.03, -88.75) * mm, "mid": v(-32.78, -88.22) * mm, "end": v(-26.54, -87.6) * mm});
            skCircle(sketch, "E422", {"center": v(-32.53, -76.43) * mm, "radius": 4.62 * mm});
            skArc(sketch, "E423", {"start": v(-56.84, -87.23) * mm, "mid": v(-47.98, -88.6) * mm, "end": v(-39.03, -88.75) * mm});
            skLineSegment(sketch, "E424", {"start": v(-57.63, -81.42) * mm, "end": v(-57.63, -86.52) * mm});
            skLineSegment(sketch, "E425", {"start": v(-25.94, -81.42) * mm, "end": v(-25.94, -86.52) * mm});
            skLineSegment(sketch, "E426", {"start": v(17.13, -57.87) * mm, "end": v(28, -51.6) * mm});
            skArc(sketch, "E427", {"start": v(17.15, -60.62) * mm, "mid": v(16.63, -44.09) * mm, "end": v(15.17, -27.62) * mm});
            skLineSegment(sketch, "E428", {"start": v(15.17, -83.13) * mm, "end": v(15.17, -82.55) * mm});
            skLineSegment(sketch, "E429", {"start": v(34.52, -70.94) * mm, "end": v(28.58, -70.94) * mm});
            skFitSpline(sketch, "E430", {"points": [v(37.54, -69.05) * mm, v(36.88, -69.5) * mm, v(35.74, -70.41) * mm, v(37.75, -71.88) * mm, v(37.18, -72.7) * mm, v(36.9, -73.01) * mm]});
            skLineSegment(sketch, "E431", {"start": v(8.57, -27.62) * mm, "end": v(9.56, -27.62) * mm});
            skLineSegment(sketch, "E432", {"start": v(7.58, -29.6) * mm, "end": v(8.57, -29.6) * mm});
            skLineSegment(sketch, "E433", {"start": v(-5.27, 39.23) * mm, "end": v(-3.11, 40.24) * mm});
            skLineSegment(sketch, "E434", {"start": v(2.65, 39.23) * mm, "end": v(-5.27, 39.23) * mm});
            skLineSegment(sketch, "E435", {"start": v(-48.82, 27.14) * mm, "end": v(47.45, 27.14) * mm});
            skArc(sketch, "E436", {"start": v(-20.48, 43.64) * mm, "mid": v(-37.85, 41.56) * mm, "end": v(-53.48, 33.74) * mm});
            skLineSegment(sketch, "E437", {"start": v(-48.82, 46.94) * mm, "end": v(-25.15, 46.94) * mm});
            skLineSegment(sketch, "E438", {"start": v(-29.73, 43.64) * mm, "end": v(-52.16, 43.64) * mm});
            skLineSegment(sketch, "E439", {"start": v(-53.48, 32.42) * mm, "end": v(-53.48, 25.97) * mm});
            skCircle(sketch, "E440", {"center": v(-14.27, 38.57) * mm, "radius": 4.62 * mm});
            skLineSegment(sketch, "E441", {"start": v(2.65, 39.23) * mm, "end": v(0.5, 38.23) * mm});
            skLineSegment(sketch, "E442", {"start": v(103.73, -5.4) * mm, "end": v(103.73, -23.53) * mm});
            skLineSegment(sketch, "E443", {"start": v(97.79, -1.48) * mm, "end": v(97.79, -22.56) * mm});
            skLineSegment(sketch, "E444", {"start": v(91.85, -5.4) * mm, "end": v(91.85, -22.17) * mm});
            skLineSegment(sketch, "E445", {"start": v(95.8, -8.17) * mm, "end": v(95.8, -22.09) * mm});
            skLineSegment(sketch, "E446", {"start": v(99.77, -8.17) * mm, "end": v(99.77, -24.02) * mm});
            skLineSegment(sketch, "E447", {"start": v(106.86, -50.15) * mm, "end": v(99, -58) * mm});
            skArc(sketch, "E448", {"start": v(99, -75.23) * mm, "mid": v(102.97, -79.19) * mm, "end": v(106.93, -75.23) * mm});
            skFitSpline(sketch, "E449", {"points": [v(89.77, -22.39) * mm, v(91.06, -22.25) * mm, v(93.35, -22) * mm, v(96.3, -22.02) * mm, v(98.5, -22.75) * mm, v(100.74, -25.41) * mm, v(103.43, -23.76) * mm, v(105.46, -22.51) * mm]});
            skLineSegment(sketch, "E450", {"start": v(102.97, -69.95) * mm, "end": v(89.77, -69.95) * mm});
            skLineSegment(sketch, "E451", {"start": v(83.81, -50.15) * mm, "end": v(102.9, -50.15) * mm});
            skLineSegment(sketch, "E452", {"start": v(94.98, -50.28) * mm, "end": v(103.04, -50.28) * mm});
            skLineSegment(sketch, "E453", {"start": v(94.98, -50.21) * mm, "end": v(102.97, -50.21) * mm});
            skLineSegment(sketch, "E454", {"start": v(90.36, -46.06) * mm, "end": v(115.44, -46.06) * mm});
            skLineSegment(sketch, "E455", {"start": v(90.36, -46.12) * mm, "end": v(115.44, -46.12) * mm});
            skLineSegment(sketch, "E456", {"start": v(82.24, -46.19) * mm, "end": v(122.94, -46.19) * mm});
            skLineSegment(sketch, "E457", {"start": v(83.17, -69.95) * mm, "end": v(56.77, -69.95) * mm});
            skLineSegment(sketch, "E458", {"start": v(66.61, -63.35) * mm, "end": v(99, -63.35) * mm});
            skLineSegment(sketch, "E459", {"start": v(52.87, -76.76) * mm, "end": v(57.08, -71.6) * mm});
            skLineSegment(sketch, "E460", {"start": v(60.43, -69.62) * mm, "end": v(59.47, -72.26) * mm});
            skLineSegment(sketch, "E461", {"start": v(61.84, -69.62) * mm, "end": v(60.88, -72.26) * mm});
            skLineSegment(sketch, "E462", {"start": v(74.48, -69.62) * mm, "end": v(73.52, -72.26) * mm});
            skLineSegment(sketch, "E463", {"start": v(73.08, -69.62) * mm, "end": v(72.12, -72.26) * mm});
            skLineSegment(sketch, "E464", {"start": v(70.27, -69.62) * mm, "end": v(69.3, -72.26) * mm});
            skLineSegment(sketch, "E465", {"start": v(71.67, -69.62) * mm, "end": v(70.71, -72.26) * mm});
            skLineSegment(sketch, "E466", {"start": v(66.05, -69.62) * mm, "end": v(65.1, -72.26) * mm});
            skLineSegment(sketch, "E467", {"start": v(64.65, -69.62) * mm, "end": v(63.69, -72.26) * mm});
            skLineSegment(sketch, "E468", {"start": v(67.46, -69.62) * mm, "end": v(66.5, -72.26) * mm});
            skLineSegment(sketch, "E469", {"start": v(68.86, -69.62) * mm, "end": v(67.9, -72.26) * mm});
            skLineSegment(sketch, "E470", {"start": v(63.24, -69.62) * mm, "end": v(62.28, -72.26) * mm});
            skLineSegment(sketch, "E471", {"start": v(99, -58) * mm, "end": v(99, -75.23) * mm});
            skLineSegment(sketch, "E472", {"start": v(86.47, -76.55) * mm, "end": v(83.17, -69.95) * mm});
            skLineSegment(sketch, "E473", {"start": v(89.77, -69.95) * mm, "end": v(86.47, -76.55) * mm});
            skLineSegment(sketch, "E474", {"start": v(76.57, -70.28) * mm, "end": v(76.57, -71.6) * mm});
            skLineSegment(sketch, "E475", {"start": v(74.29, -43.37) * mm, "end": v(86.84, -43.37) * mm});
            skLineSegment(sketch, "E476", {"start": v(86.84, -43.37) * mm, "end": v(89.6, -46.74) * mm});
            skLineSegment(sketch, "E477", {"start": v(75.6, -56.19) * mm, "end": v(94.4, -56.19) * mm});
            skFitSpline(sketch, "E478", {"points": [v(84.26, -44.4) * mm, v(82.94, -45.3) * mm, v(80.66, -47.12) * mm, v(84.67, -50.05) * mm, v(83.54, -51.7) * mm, v(82.97, -52.32) * mm]});
            skLineSegment(sketch, "E479", {"start": v(94.4, -56.19) * mm, "end": v(99.22, -50.28) * mm});
            skLineSegment(sketch, "E480", {"start": v(116.17, -50.15) * mm, "end": v(106.93, -59.39) * mm});
            skLineSegment(sketch, "E481", {"start": v(106.93, -59.39) * mm, "end": v(106.93, -75.23) * mm});
            skCircle(sketch, "E482", {"center": v(102.97, -75.23) * mm, "radius": 0.53 * mm});
            skCircle(sketch, "E483", {"center": v(102.97, -64.67) * mm, "radius": 0.53 * mm});
            skCircle(sketch, "E484", {"center": v(102.97, -69.95) * mm, "radius": 0.53 * mm});
            skLineSegment(sketch, "E485", {"start": v(135.62, -67.22) * mm, "end": v(132.32, -67.22) * mm});
            skLineSegment(sketch, "E486", {"start": v(133.97, -65.57) * mm, "end": v(133.97, -68.87) * mm});
            skLineSegment(sketch, "E487", {"start": v(120.47, -43.37) * mm, "end": v(136.12, -43.37) * mm});
            skLineSegment(sketch, "E488", {"start": v(110.84, -39.25) * mm, "end": v(129.51, -39.25) * mm});
            skLineSegment(sketch, "E489", {"start": v(110.84, -39.25) * mm, "end": v(105.28, -46.06) * mm});
            skLineSegment(sketch, "E490", {"start": v(106.86, -50.15) * mm, "end": v(121.37, -50.15) * mm});
            skLineSegment(sketch, "E491", {"start": v(106.8, -50.28) * mm, "end": v(114.78, -50.28) * mm});
            skLineSegment(sketch, "E492", {"start": v(106.84, -50.21) * mm, "end": v(114.78, -50.21) * mm});
            skLineSegment(sketch, "E493", {"start": v(102.9, -46.19) * mm, "end": v(106.86, -50.15) * mm});
            skLineSegment(sketch, "E494", {"start": v(102.9, -46.19) * mm, "end": v(102.9, -50.15) * mm});
            skLineSegment(sketch, "E495", {"start": v(103.04, -46.5) * mm, "end": v(106.8, -50.28) * mm});
            skLineSegment(sketch, "E496", {"start": v(103.04, -46.5) * mm, "end": v(103.04, -50.28) * mm});
            skLineSegment(sketch, "E497", {"start": v(102.97, -46.35) * mm, "end": v(102.97, -50.21) * mm});
            skLineSegment(sketch, "E498", {"start": v(102.97, -46.35) * mm, "end": v(106.84, -50.21) * mm});
            skLineSegment(sketch, "E499", {"start": v(120.47, -43.37) * mm, "end": v(117.72, -46.74) * mm});
            skFitSpline(sketch, "E500", {"points": [v(120.93, -44.4) * mm, v(122.24, -45.3) * mm, v(124.52, -47.12) * mm, v(120.51, -50.05) * mm, v(121.64, -51.7) * mm, v(122.21, -52.32) * mm]});
            skLineSegment(sketch, "E501", {"start": v(116.17, -46.19) * mm, "end": v(116.17, -50.15) * mm});
            skLineSegment(sketch, "E502", {"start": v(98.97, -14.46) * mm, "end": v(110.2, -6.61) * mm});
            skLineSegment(sketch, "E503", {"start": v(109.67, -17.01) * mm, "end": v(85.9, -17.01) * mm});
            skLineSegment(sketch, "E504", {"start": v(100.82, -9.04) * mm, "end": v(103.9, -13.44) * mm});
            skLineSegment(sketch, "E505", {"start": v(114.18, 1.92) * mm, "end": v(99.77, -8.17) * mm});
            skLineSegment(sketch, "E506", {"start": v(103.73, -5.4) * mm, "end": v(98.26, -5.4) * mm});
            skLineSegment(sketch, "E507", {"start": v(112.59, 5.64) * mm, "end": v(97.79, -4.72) * mm});
            skLineSegment(sketch, "E508", {"start": v(117.87, 22.82) * mm, "end": v(77.7, 22.82) * mm});
            skLineSegment(sketch, "E509", {"start": v(73.04, 29.42) * mm, "end": v(73.04, -2.92) * mm});
            skLineSegment(sketch, "E510", {"start": v(81.4, 1.92) * mm, "end": v(95.8, -8.17) * mm});
            skLineSegment(sketch, "E511", {"start": v(82.65, -0.77) * mm, "end": v(82.65, -12.17) * mm});
            skLineSegment(sketch, "E512", {"start": v(83, 5.64) * mm, "end": v(97.79, -4.72) * mm});
            skLineSegment(sketch, "E513", {"start": v(89.9, -5.4) * mm, "end": v(81.33, -5.4) * mm});
            skLineSegment(sketch, "E514", {"start": v(91.11, -6.49) * mm, "end": v(88.04, -10.88) * mm});
            skLineSegment(sketch, "E515", {"start": v(96.6, -14.46) * mm, "end": v(85.39, -6.61) * mm});
            skLineSegment(sketch, "E516", {"start": v(85.29, -7.55) * mm, "end": v(81.33, -7.55) * mm});
            skLineSegment(sketch, "E517", {"start": v(99.77, -8.17) * mm, "end": v(99.77, -7.55) * mm});
            skLineSegment(sketch, "E518", {"start": v(95.8, -8.17) * mm, "end": v(95.8, -7.55) * mm});
            skLineSegment(sketch, "E519", {"start": v(97.32, -5.4) * mm, "end": v(98.26, -5.4) * mm});
            skLineSegment(sketch, "E520", {"start": v(97.32, -5.4) * mm, "end": v(91.85, -5.4) * mm});
            skLineSegment(sketch, "E521", {"start": v(97.79, -4.72) * mm, "end": v(100.06, -7.96) * mm});
            skLineSegment(sketch, "E522", {"start": v(95.52, -7.96) * mm, "end": v(97.79, -4.72) * mm});
            skLineSegment(sketch, "E523", {"start": v(94.76, -9.04) * mm, "end": v(91.69, -13.44) * mm});
            skFitSpline(sketch, "E524", {"points": [v(80.19, 1.6) * mm, v(80.52, 1.69) * mm, v(81.26, 1.89) * mm, v(82.53, 2.22) * mm, v(82.68, 3.64) * mm, v(81.76, 4.74) * mm, v(82.75, 5.52) * mm, v(83.47, 5.9) * mm, v(83.93, 6.17) * mm, v(84.18, 6.32) * mm]});
            skLineSegment(sketch, "E525", {"start": v(94.02, -0.82) * mm, "end": v(101.56, -0.82) * mm});
            skLineSegment(sketch, "E526", {"start": v(98.26, -3.46) * mm, "end": v(98.26, 0.5) * mm});
            skLineSegment(sketch, "E527", {"start": v(97.32, -3.46) * mm, "end": v(97.32, 0.5) * mm});
            skArc(sketch, "E528", {"start": v(102.13, 3.84) * mm, "mid": v(97.79, 4.88) * mm, "end": v(93.45, 3.84) * mm});
            skLineSegment(sketch, "E529", {"start": v(52.12, 32.42) * mm, "end": v(52.12, 25.97) * mm});
            skLineSegment(sketch, "E530", {"start": v(122.54, 16.22) * mm, "end": v(122.54, 10.28) * mm});
            skLineSegment(sketch, "E531", {"start": v(128.38, 25.55) * mm, "end": v(128.38, 0.94) * mm});
            skLineSegment(sketch, "E532", {"start": v(131.04, 10.28) * mm, "end": v(125.72, 10.28) * mm});
            skLineSegment(sketch, "E533", {"start": v(112.93, -0.77) * mm, "end": v(112.93, -12.79) * mm});
            skLineSegment(sketch, "E534", {"start": v(109.63, -8.17) * mm, "end": v(114.25, -8.17) * mm});
            skLineSegment(sketch, "E535", {"start": v(105.67, -5.4) * mm, "end": v(114.25, -5.4) * mm});
            skLineSegment(sketch, "E536", {"start": v(104.47, -6.49) * mm, "end": v(107.54, -10.88) * mm});
            skFitSpline(sketch, "E537", {"points": [v(115.4, 1.6) * mm, v(115.06, 1.69) * mm, v(114.32, 1.89) * mm, v(113.05, 2.22) * mm, v(112.9, 3.64) * mm, v(113.82, 4.74) * mm, v(112.83, 5.52) * mm, v(112.1, 5.9) * mm, v(111.65, 6.17) * mm, v(111.4, 6.32) * mm]});
            skLineSegment(sketch, "E538", {"start": v(122.54, 10.28) * mm, "end": v(122.54, -2.92) * mm});
            skLineSegment(sketch, "E539", {"start": v(131.04, 16.22) * mm, "end": v(125.72, 16.22) * mm});
            skLineSegment(sketch, "E540", {"start": v(122.54, 16.22) * mm, "end": v(122.54, 29.42) * mm});
            skLineSegment(sketch, "E541", {"start": v(135.05, 24.76) * mm, "end": v(135.74, 27.02) * mm});
            skLineSegment(sketch, "E542", {"start": v(148.27, 45.48) * mm, "end": v(143.6, 45.48) * mm});
            skArc(sketch, "E543", {"start": v(13.6, 94.41) * mm, "mid": v(42.96, 87.43) * mm, "end": v(73.04, 85.08) * mm});
            skArc(sketch, "E544", {"start": v(10.34, 61.98) * mm, "mid": v(36.66, 59.13) * mm, "end": v(63.14, 58.68) * mm});
            skLineSegment(sketch, "E545", {"start": v(-35.86, 63.3) * mm, "end": v(-35.86, 55.73) * mm});
            skArc(sketch, "E546", {"start": v(13.6, 94.41) * mm, "mid": v(6.89, 97.38) * mm, "end": v(0.09, 100.16) * mm});
            skLineSegment(sketch, "E547", {"start": v(-35.28, 121.38) * mm, "end": v(11.5, 121.38) * mm});
            skLineSegment(sketch, "E548", {"start": v(148.58, 124.68) * mm, "end": v(148.58, 75.18) * mm});
            skLineSegment(sketch, "E549", {"start": v(133.14, 124.68) * mm, "end": v(133.14, 52.08) * mm});
            skLineSegment(sketch, "E550", {"start": v(146.34, 124.68) * mm, "end": v(146.34, 75.18) * mm});
            skLineSegment(sketch, "E551", {"start": v(122.54, 87.06) * mm, "end": v(122.54, 136.56) * mm});
            skLineSegment(sketch, "E552", {"start": v(139.74, 120.02) * mm, "end": v(139.74, 79.85) * mm});
            skLineSegment(sketch, "E553", {"start": v(73.04, 85.08) * mm, "end": v(122.54, 85.08) * mm});
            skArc(sketch, "E554", {"start": v(63.14, 58.68) * mm, "mid": v(87.92, 59.87) * mm, "end": v(112.64, 61.98) * mm});
            skLineSegment(sketch, "E555", {"start": v(145.64, 85.08) * mm, "end": v(145.64, 71.88) * mm});
            skLineSegment(sketch, "E556", {"start": v(122.54, 85.08) * mm, "end": v(122.54, 71.88) * mm});
            skArc(sketch, "E557", {"start": v(112.64, 61.98) * mm, "mid": v(119.34, 65.18) * mm, "end": v(122.54, 71.88) * mm});
            skLineSegment(sketch, "E558", {"start": v(139.74, 70.52) * mm, "end": v(139.74, 52.08) * mm});
            skLineSegment(sketch, "E559", {"start": v(151.62, 52.08) * mm, "end": v(131.16, 52.08) * mm});
            skLineSegment(sketch, "E560", {"start": v(151.62, 52.08) * mm, "end": v(143.85, 52.08) * mm});
            skLineSegment(sketch, "E561", {"start": v(145.02, 75.18) * mm, "end": v(138.57, 75.18) * mm});
            skLineSegment(sketch, "E562", {"start": v(152.94, 75.18) * mm, "end": v(152.94, 81.45) * mm});
            skLineSegment(sketch, "E563", {"start": v(152.94, 75.18) * mm, "end": v(152.94, 68.58) * mm});
            skLineSegment(sketch, "E564", {"start": v(140.4, 84.82) * mm, "end": v(154.52, 84.82) * mm});
            skLineSegment(sketch, "E565", {"start": v(154.15, 96.65) * mm, "end": v(154.15, 91.98) * mm});
            skLineSegment(sketch, "E566", {"start": v(154.15, 107.92) * mm, "end": v(154.15, 101.32) * mm});
            skLineSegment(sketch, "E567", {"start": v(154.15, 112.58) * mm, "end": v(154.15, 117.25) * mm});
            skLineSegment(sketch, "E568", {"start": v(146.34, 126) * mm, "end": v(146.34, 135.75) * mm});
            skLineSegment(sketch, "E569", {"start": v(145.02, 124.68) * mm, "end": v(131.16, 124.68) * mm});
            skLineSegment(sketch, "E570", {"start": v(146.34, 126) * mm, "end": v(146.34, 129.15) * mm});
            skLineSegment(sketch, "E571", {"start": v(159.54, 50.76) * mm, "end": v(159.54, 44.32) * mm});
            skLineSegment(sketch, "E572", {"start": v(278.34, 48.2) * mm, "end": v(278.34, 37.72) * mm});
            skLineSegment(sketch, "E573", {"start": v(266, -48.04) * mm, "end": v(242.03, -48.04) * mm});
            skLineSegment(sketch, "E574", {"start": v(197.81, -29.23) * mm, "end": v(263.81, -29.23) * mm});
            skLineSegment(sketch, "E575", {"start": v(262.16, -41.44) * mm, "end": v(272.92, -41.44) * mm});
            skLineSegment(sketch, "E576", {"start": v(253.87, -35.83) * mm, "end": v(270.46, -35.83) * mm});
            skLineSegment(sketch, "E577", {"start": v(260.51, -43.42) * mm, "end": v(263.81, -43.42) * mm});
            skLineSegment(sketch, "E578", {"start": v(240.58, 13.2) * mm, "end": v(276.8, 13.2) * mm});
            skLineSegment(sketch, "E579", {"start": v(276.8, 24.76) * mm, "end": v(238.93, 13.2) * mm});
            skLineSegment(sketch, "E580", {"start": v(276.12, 27.02) * mm, "end": v(238.93, 15.68) * mm});
            skLineSegment(sketch, "E581", {"start": v(164.2, 45.48) * mm, "end": v(278.34, 45.48) * mm});
            skLineSegment(sketch, "E582", {"start": v(273.67, 38.88) * mm, "end": v(157.6, 38.88) * mm});
            skLineSegment(sketch, "E583", {"start": v(222.23, -50.83) * mm, "end": v(195.83, -50.83) * mm});
            skLineSegment(sketch, "E584", {"start": v(207.71, -41.44) * mm, "end": v(220.91, -41.44) * mm});
            skLineSegment(sketch, "E585", {"start": v(157.07, -27.62) * mm, "end": v(183.47, -27.62) * mm});
            skLineSegment(sketch, "E586", {"start": v(194.51, -53.37) * mm, "end": v(194.51, -34.03) * mm});
            skLineSegment(sketch, "E587", {"start": v(190.55, -41.44) * mm, "end": v(196.5, -41.44) * mm});
            skLineSegment(sketch, "E588", {"start": v(190.55, -46.06) * mm, "end": v(196.5, -46.06) * mm});
            skLineSegment(sketch, "E589", {"start": v(197.81, -41.44) * mm, "end": v(197.81, -46.06) * mm});
            skLineSegment(sketch, "E590", {"start": v(206.06, -44.74) * mm, "end": v(207.71, -41.44) * mm});
            skLineSegment(sketch, "E591", {"start": v(204.41, -41.44) * mm, "end": v(206.06, -44.74) * mm});
            skLineSegment(sketch, "E592", {"start": v(197.81, -47.56) * mm, "end": v(197.81, -52.81) * mm});
            skLineSegment(sketch, "E593", {"start": v(197.81, -41.44) * mm, "end": v(204.41, -41.44) * mm});
            skLineSegment(sketch, "E594", {"start": v(197.81, -39.2) * mm, "end": v(197.81, -28.06) * mm});
            skLineSegment(sketch, "E595", {"start": v(234.21, -40.45) * mm, "end": v(253.91, -40.45) * mm});
            skLineSegment(sketch, "E596", {"start": v(234.68, -41.11) * mm, "end": v(253.91, -41.11) * mm});
            skFitSpline(sketch, "E597", {"points": [v(235.25, -38.8) * mm, v(234.6, -39.25) * mm, v(233.45, -40.16) * mm, v(235.46, -41.63) * mm, v(234.9, -42.46) * mm, v(234.6, -42.76) * mm]});
            skFitSpline(sketch, "E598", {"points": [v(231.9, -38.8) * mm, v(231.24, -39.25) * mm, v(230.1, -40.16) * mm, v(232.1, -41.63) * mm, v(231.53, -42.46) * mm, v(231.25, -42.76) * mm]});
            skLineSegment(sketch, "E599", {"start": v(211.01, -40.45) * mm, "end": v(230.85, -40.45) * mm});
            skLineSegment(sketch, "E600", {"start": v(211.01, -41.11) * mm, "end": v(231.33, -41.11) * mm});
            skLineSegment(sketch, "E601", {"start": v(211.01, -47.53) * mm, "end": v(211.01, -52.81) * mm});
            skLineSegment(sketch, "E602", {"start": v(220.91, -47.53) * mm, "end": v(220.91, -52.81) * mm});
            skLineSegment(sketch, "E603", {"start": v(217.74, -41.77) * mm, "end": v(218.46, -39.8) * mm});
            skLineSegment(sketch, "E604", {"start": v(218.44, -41.77) * mm, "end": v(219.16, -39.8) * mm});
            skLineSegment(sketch, "E605", {"start": v(219.14, -41.77) * mm, "end": v(219.86, -39.8) * mm});
            skLineSegment(sketch, "E606", {"start": v(214.93, -41.77) * mm, "end": v(215.65, -39.8) * mm});
            skLineSegment(sketch, "E607", {"start": v(215.63, -41.77) * mm, "end": v(216.35, -39.8) * mm});
            skLineSegment(sketch, "E608", {"start": v(217.03, -41.77) * mm, "end": v(217.75, -39.8) * mm});
            skLineSegment(sketch, "E609", {"start": v(216.33, -41.77) * mm, "end": v(217.05, -39.8) * mm});
            skLineSegment(sketch, "E610", {"start": v(213.52, -41.77) * mm, "end": v(214.24, -39.8) * mm});
            skLineSegment(sketch, "E611", {"start": v(214.22, -41.77) * mm, "end": v(214.94, -39.8) * mm});
            skLineSegment(sketch, "E612", {"start": v(212.82, -41.77) * mm, "end": v(213.54, -39.8) * mm});
            skLineSegment(sketch, "E613", {"start": v(212.12, -41.77) * mm, "end": v(212.84, -39.8) * mm});
            skLineSegment(sketch, "E614", {"start": v(211.01, -41.11) * mm, "end": v(211.01, -40.45) * mm});
            skLineSegment(sketch, "E615", {"start": v(250, -41.77) * mm, "end": v(249.28, -39.8) * mm});
            skLineSegment(sketch, "E616", {"start": v(244.01, -41.44) * mm, "end": v(260.51, -41.44) * mm});
            skLineSegment(sketch, "E617", {"start": v(244.01, -42.76) * mm, "end": v(244.01, -51.34) * mm});
            skLineSegment(sketch, "E618", {"start": v(248.6, -41.77) * mm, "end": v(247.87, -39.8) * mm});
            skLineSegment(sketch, "E619", {"start": v(247.9, -41.77) * mm, "end": v(247.17, -39.8) * mm});
            skLineSegment(sketch, "E620", {"start": v(249.3, -41.77) * mm, "end": v(248.58, -39.8) * mm});
            skLineSegment(sketch, "E621", {"start": v(245.78, -41.77) * mm, "end": v(245.06, -39.8) * mm});
            skLineSegment(sketch, "E622", {"start": v(246.49, -41.77) * mm, "end": v(245.77, -39.8) * mm});
            skLineSegment(sketch, "E623", {"start": v(247.19, -41.77) * mm, "end": v(246.47, -39.8) * mm});
            skLineSegment(sketch, "E624", {"start": v(260.51, -44.74) * mm, "end": v(260.51, -51.34) * mm});
            skLineSegment(sketch, "E625", {"start": v(253.91, -42.76) * mm, "end": v(253.91, -51.34) * mm});
            skLineSegment(sketch, "E626", {"start": v(252.8, -41.77) * mm, "end": v(252.09, -39.8) * mm});
            skLineSegment(sketch, "E627", {"start": v(252.1, -41.77) * mm, "end": v(251.39, -39.8) * mm});
            skLineSegment(sketch, "E628", {"start": v(250.7, -41.77) * mm, "end": v(249.98, -39.8) * mm});
            skLineSegment(sketch, "E629", {"start": v(251.4, -41.77) * mm, "end": v(250.68, -39.8) * mm});
            skLineSegment(sketch, "E630", {"start": v(253.91, -41.11) * mm, "end": v(253.91, -40.45) * mm});
            skLineSegment(sketch, "E631", {"start": v(260.51, -41.44) * mm, "end": v(260.51, -43.42) * mm});
            skLineSegment(sketch, "E632", {"start": v(260.51, -39.2) * mm, "end": v(260.51, -34.66) * mm});
            skCircle(sketch, "E633", {"center": v(205.93, 5.27) * mm, "radius": 10.48 * mm});
            skArc(sketch, "E634", {"start": v(225.3, 22.53) * mm, "mid": v(205.93, 30.6) * mm, "end": v(186.55, 22.53) * mm});
            skLineSegment(sketch, "E635", {"start": v(208.63, 4.57) * mm, "end": v(210.24, 2.27) * mm});
            skLineSegment(sketch, "E636", {"start": v(208.77, 4.67) * mm, "end": v(210.38, 2.37) * mm});
            skLineSegment(sketch, "E637", {"start": v(220.1, 13.2) * mm, "end": v(206.67, 3.8) * mm});
            skLineSegment(sketch, "E638", {"start": v(220.97, 13.2) * mm, "end": v(206.67, 3.2) * mm});
            skLineSegment(sketch, "E639", {"start": v(172.93, 15.68) * mm, "end": v(238.93, 15.68) * mm});
            skLineSegment(sketch, "E640", {"start": v(172.93, 13.2) * mm, "end": v(238.93, 13.2) * mm});
            skLineSegment(sketch, "E641", {"start": v(208.4, 13.2) * mm, "end": v(208.4, 12.88) * mm});
            skLineSegment(sketch, "E642", {"start": v(203.45, 13.2) * mm, "end": v(203.45, 12.88) * mm});
            skLineSegment(sketch, "E643", {"start": v(191.75, 13.2) * mm, "end": v(205.19, 3.8) * mm});
            skLineSegment(sketch, "E644", {"start": v(190.9, 13.2) * mm, "end": v(205.19, 3.2) * mm});
            skLineSegment(sketch, "E645", {"start": v(205.93, 16.67) * mm, "end": v(205.93, -7.91) * mm});
            skLineSegment(sketch, "E646", {"start": v(205.19, 12.88) * mm, "end": v(205.19, -6.92) * mm});
            skLineSegment(sketch, "E647", {"start": v(206.67, 12.88) * mm, "end": v(206.67, -6.92) * mm});
            skLineSegment(sketch, "E648", {"start": v(205.19, -6.92) * mm, "end": v(206.67, -6.92) * mm});
            skLineSegment(sketch, "E649", {"start": v(203.45, 12.88) * mm, "end": v(208.4, 12.88) * mm});
            skLineSegment(sketch, "E650", {"start": v(208.4, 11.56) * mm, "end": v(208.4, 10.9) * mm});
            skLineSegment(sketch, "E651", {"start": v(206.67, 11.56) * mm, "end": v(208.4, 11.56) * mm});
            skLineSegment(sketch, "E652", {"start": v(206.67, 10.9) * mm, "end": v(208.4, 10.9) * mm});
            skLineSegment(sketch, "E653", {"start": v(203.45, 11.56) * mm, "end": v(205.19, 11.56) * mm});
            skLineSegment(sketch, "E654", {"start": v(203.45, 10.9) * mm, "end": v(205.19, 10.9) * mm});
            skLineSegment(sketch, "E655", {"start": v(203.45, 11.56) * mm, "end": v(203.45, 10.9) * mm});
            skLineSegment(sketch, "E656", {"start": v(201.48, 2.37) * mm, "end": v(201.62, 2.27) * mm});
            skLineSegment(sketch, "E657", {"start": v(203.1, 4.67) * mm, "end": v(201.48, 2.37) * mm});
            skLineSegment(sketch, "E658", {"start": v(203.23, 4.57) * mm, "end": v(201.62, 2.27) * mm});
            skLineSegment(sketch, "E659", {"start": v(178.9, 22.21) * mm, "end": v(188.22, 15.68) * mm});
            skLineSegment(sketch, "E660", {"start": v(178.61, 21.8) * mm, "end": v(187.36, 15.68) * mm});
            skLineSegment(sketch, "E661", {"start": v(178.9, 22.21) * mm, "end": v(178.61, 21.8) * mm});
            skLineSegment(sketch, "E662", {"start": v(172.93, 15.68) * mm, "end": v(172.93, 13.2) * mm});
            skLineSegment(sketch, "E663", {"start": v(210.38, 2.37) * mm, "end": v(210.24, 2.27) * mm});
            skLineSegment(sketch, "E664", {"start": v(232.96, 22.21) * mm, "end": v(233.25, 21.8) * mm});
            skLineSegment(sketch, "E665", {"start": v(233.25, 21.8) * mm, "end": v(224.5, 15.68) * mm});
            skLineSegment(sketch, "E666", {"start": v(232.96, 22.21) * mm, "end": v(223.64, 15.68) * mm});
            skLineSegment(sketch, "E667", {"start": v(238.93, 15.68) * mm, "end": v(238.93, 13.2) * mm});
            skCircle(sketch, "E668", {"center": v(271.2, -26.43) * mm, "radius": 4.62 * mm});
            skLineSegment(sketch, "E669", {"start": v(271.76, -52.05) * mm, "end": v(271.76, -35.5) * mm});
            skLineSegment(sketch, "E670", {"start": v(265.13, -43.42) * mm, "end": v(272.92, -43.42) * mm});
            skLineSegment(sketch, "E671", {"start": v(263.81, -39.2) * mm, "end": v(263.81, -28.06) * mm});
            skLineSegment(sketch, "E672", {"start": v(276.8, 24.76) * mm, "end": v(276.12, 27.02) * mm});
            skLineSegment(sketch, "E673", {"start": v(276.8, 24.76) * mm, "end": v(276.8, 13.2) * mm});
            skLineSegment(sketch, "E674", {"start": v(238.74, 85.08) * mm, "end": v(266.74, 113.09) * mm});
            skArc(sketch, "E675", {"start": v(278.34, 85.08) * mm, "mid": v(266.74, 113.09) * mm, "end": v(238.74, 124.68) * mm});
            skLineSegment(sketch, "E676", {"start": v(159.54, 52.08) * mm, "end": v(278.34, 52.08) * mm});
            skCircle(sketch, "E677", {"center": v(260.18, 86.7) * mm, "radius": 4.62 * mm});
            skLineSegment(sketch, "E678", {"start": v(177.25, 111.49) * mm, "end": v(177.25, 118.98) * mm});
            skLineSegment(sketch, "E679", {"start": v(160.75, 108.5) * mm, "end": v(160.75, 118.98) * mm});
            skLineSegment(sketch, "E680", {"start": v(160.2, 68.58) * mm, "end": v(160.2, 75.18) * mm});
            skLineSegment(sketch, "E681", {"start": v(159.54, 68.58) * mm, "end": v(160.2, 68.58) * mm});
            skLineSegment(sketch, "E682", {"start": v(159.54, 75.18) * mm, "end": v(159.54, 68.58) * mm});
            skLineSegment(sketch, "E683", {"start": v(181.25, 116.5) * mm, "end": v(181.25, 99.34) * mm});
            skLineSegment(sketch, "E684", {"start": v(162.73, 100.73) * mm, "end": v(162.73, 93.55) * mm});
            skLineSegment(sketch, "E685", {"start": v(160.75, 100.73) * mm, "end": v(160.75, 93.55) * mm});
            skCircle(sketch, "E686", {"center": v(177.27, 94.04) * mm, "radius": 4.62 * mm});
            skLineSegment(sketch, "E687", {"start": v(169, 107.92) * mm, "end": v(170.98, 107.92) * mm});
            skLineSegment(sketch, "E688", {"start": v(166.65, 109.9) * mm, "end": v(175.27, 109.9) * mm});
            skLineSegment(sketch, "E689", {"start": v(167.35, 105.94) * mm, "end": v(175.27, 105.94) * mm});
            skLineSegment(sketch, "E690", {"start": v(165.41, 117.82) * mm, "end": v(177.25, 117.82) * mm});
            skLineSegment(sketch, "E691", {"start": v(162.73, 105.97) * mm, "end": v(166.65, 109.9) * mm});
            skLineSegment(sketch, "E692", {"start": v(160.75, 107.95) * mm, "end": v(162.73, 105.97) * mm});
            skLineSegment(sketch, "E693", {"start": v(160.75, 101.32) * mm, "end": v(162.73, 101.32) * mm});
            skLineSegment(sketch, "E694", {"start": v(162.73, 101.32) * mm, "end": v(167.35, 105.94) * mm});
            skLineSegment(sketch, "E695", {"start": v(160.75, 107.95) * mm, "end": v(160.75, 101.32) * mm});
            skArc(sketch, "E696", {"start": v(175.27, 105.94) * mm, "mid": v(177.25, 107.92) * mm, "end": v(175.27, 109.9) * mm});
            skCircle(sketch, "E697", {"center": v(175.27, 107.92) * mm, "radius": 0.26 * mm});
            skLineSegment(sketch, "E698", {"start": v(174.28, 107.92) * mm, "end": v(176.26, 107.92) * mm});
            skLineSegment(sketch, "E699", {"start": v(175.27, 108.9) * mm, "end": v(175.27, 106.93) * mm});
            skLineSegment(sketch, "E700", {"start": v(177.95, 109.9) * mm, "end": v(182.57, 109.9) * mm});
            skLineSegment(sketch, "E701", {"start": v(177.95, 105.94) * mm, "end": v(182.57, 105.94) * mm});
            skLineSegment(sketch, "E702", {"start": v(172.63, 108.9) * mm, "end": v(172.63, 106.93) * mm});
            skCircle(sketch, "E703", {"center": v(169.99, 107.92) * mm, "radius": 0.26 * mm});
            skLineSegment(sketch, "E704", {"start": v(169.99, 108.9) * mm, "end": v(169.99, 106.93) * mm});
            skLineSegment(sketch, "E705", {"start": v(171.64, 107.92) * mm, "end": v(173.62, 107.92) * mm});
            skCircle(sketch, "E706", {"center": v(172.63, 107.92) * mm, "radius": 0.26 * mm});
            skCircle(sketch, "E707", {"center": v(222.35, 63) * mm, "radius": 4.62 * mm});
            skLineSegment(sketch, "E708", {"start": v(223.55, 95.97) * mm, "end": v(221.4, 94.97) * mm});
            skLineSegment(sketch, "E709", {"start": v(223.55, 95.97) * mm, "end": v(215.63, 95.97) * mm});
            skLineSegment(sketch, "E710", {"start": v(215.63, 95.97) * mm, "end": v(217.78, 96.98) * mm});
            skCircle(sketch, "E711", {"center": v(219.17, 108.53) * mm, "radius": 4.62 * mm});
            skLineSegment(sketch, "E712", {"start": v(238.74, 86.73) * mm, "end": v(238.74, 83.43) * mm});
            skLineSegment(sketch, "E713", {"start": v(240.39, 85.08) * mm, "end": v(237.09, 85.08) * mm});
            skLineSegment(sketch, "E714", {"start": v(228.84, 126) * mm, "end": v(228.84, 131.28) * mm});
            skLineSegment(sketch, "E715", {"start": v(278.34, 115.02) * mm, "end": v(278.34, 135.75) * mm});
            skLineSegment(sketch, "E716", {"start": v(278.34, 85.08) * mm, "end": v(278.34, 52.08) * mm});
            skLineSegment(sketch, "E717", {"start": v(282.47, 49.6) * mm, "end": v(285.77, 49.6) * mm});
            skLineSegment(sketch, "E718.trimOffspring", {"start": v(53.24, 85.08) * mm, "end": v(53.24, 86.1) * mm});
            skPoint(sketch, "E719.end.orphan", {"position": v(122.54, 134.58) * mm});
            skPoint(sketch, "E719.start.orphan", {"position": v(-240.46, 134.58) * mm});
            skLineSegment(sketch, "E720.trimOffspring", {"start": v(-82.06, 114.78) * mm, "end": v(-82.06, 120.06) * mm});
            skLineSegment(sketch, "E721.trimOffspring", {"start": v(-179.82, 114.78) * mm, "end": v(-177.76, 114.78) * mm});
            skCircle(sketch, "E722", {"center": v(-177.42, 55.42) * mm, "radius": 19.8 * mm});
            skPoint(sketch, "E722.third.point", {"position": v(-174.46, 35.84) * mm});
            skCircle(sketch, "E723.0", {"center": v(-177.42, 55.42) * mm, "radius": 22.8 * mm});
            skLineSegment(sketch, "E724", {"start": v(-197.09, 57.71) * mm, "end": v(-197.09, 31.77) * mm, "construction": true});
            skSolve(sketch);
        }
        {
            var Q0;
            {var subQ19=sQuery(id+"F0.wireOp",EDGE,"E313");Q0=makeQuery(id+"F0.imprint","IMPRINT",FACE,{"disambiguationData":[TD([[makeQuery(id+"F0.imprint","IMPRINT",EDGE,{"derivedFrom":subQ19}),-1.0]])]});}
            var Q1;
            {var subQ0=sQuery(id+"F0.wireOp",EDGE,"E313");Q1=makeQuery(id+"F0.imprint","IMPRINT",FACE,{"disambiguationData":[TD([[makeQuery(id+"F0.imprint","IMPRINT",EDGE,{"derivedFrom":subQ0}),1.0]])]});}
            var Q2;
            Q2=makeQuery(id+"F0.imprint","IMPRINT",FACE,{"disambiguationData":[TD([[makeQuery(id+"F0.imprint","IMPRINT",EDGE,{"derivedFrom":sQuery(id+"F0.wireOp",EDGE,"E133")}),-1.0]])]});
            var Q3;
            {var subQ0=sQuery(id+"F0.wireOp",EDGE,"E137");var subQ1=sQuery(id+"F0.wireOp",EDGE,"E124");var subQ2=makeQuery(id+"F0.imprint","INTERSECT",VERTEX,{"derivedFrom":[subQ1,subQ0]});Q3=makeQuery(id+"F0.imprint","IMPRINT",FACE,{"disambiguationData":[TD([[makeQuery(id+"F0.imprint","IMPRINT",EDGE,{"disambiguationData":[TD([[subQ2,-1.0]])],"derivedFrom":subQ1}),-1.0]])]});}
            var Q4;
            {var subQ0=sQuery(id+"F0.wireOp",EDGE,"E376");var subQ1=sQuery(id+"F0.wireOp",EDGE,"E124");var subQ2=makeQuery(id+"F0.imprint","INTERSECT",VERTEX,{"derivedFrom":[subQ1,subQ0]});Q4=makeQuery(id+"F0.imprint","IMPRINT",FACE,{"disambiguationData":[TD([[makeQuery(id+"F0.imprint","IMPRINT",EDGE,{"disambiguationData":[TD([[subQ2,1.0]])],"derivedFrom":subQ1}),-1.0]])]});}
            var Q5;
            {var subQ5=sQuery(id+"F0.wireOp",EDGE,"E314");var subQ10=makeQuery(id+"F0.imprint","IMPRINT",VERTEX,{"disambiguationData":[OD(0.0)],"derivedFrom":subQ5});Q5=makeQuery(id+"F0.imprint","IMPRINT",FACE,{"disambiguationData":[TD([[makeQuery(id+"F0.imprint","IMPRINT",EDGE,{"disambiguationData":[TD([[subQ10,-1.0]])],"derivedFrom":subQ5}),1.0]])]});}
            extrude(context, id + "F1", {"entities" : qUnion([Q0, Q1, Q2, Q3, Q4, Q5]), "depth" : 6 * mm});
        }
        {
            var Q0;
            Q0=sQuery(id+"F0.wireOp",VERTEX,"E359.end");
            var Q1;
            Q1=makeQuery(id+"F1.opExtrude","SWEPT_BODY",BODY,{"disambiguationData":[OSD([sQuery(id+"F0.wireOp",EDGE,"E127"),sQuery(id+"F0.wireOp",EDGE,"E133"),sQuery(id+"F0.wireOp",EDGE,"E137"),sQuery(id+"F0.wireOp",EDGE,"E139"),sQuery(id+"F0.wireOp",EDGE,"E233"),sQuery(id+"F0.wireOp",EDGE,"E315"),sQuery(id+"F0.wireOp",EDGE,"E328"),sQuery(id+"F0.wireOp",EDGE,"E331"),sQuery(id+"F0.wireOp",EDGE,"E332"),sQuery(id+"F0.wireOp",EDGE,"E355"),sQuery(id+"F0.wireOp",EDGE,"E357"),sQuery(id+"F0.wireOp",EDGE,"E376"),sQuery(id+"F0.wireOp",EDGE,"E377"),sQuery(id+"F0.wireOp",EDGE,"E543"),sQuery(id+"F0.wireOp",EDGE,"E544"),sQuery(id+"F0.wireOp",EDGE,"E546"),sQuery(id+"F0.wireOp",EDGE,"E553"),sQuery(id+"F0.wireOp",EDGE,"E554"),sQuery(id+"F0.wireOp",EDGE,"E556"),sQuery(id+"F0.wireOp",EDGE,"E557"),sQuery(id+"F0.wireOp",EDGE,"E722")])]});
            hole(context, id + "F2", {"style" : HoleStyle.SIMPLE, "endStyle" : HoleEndStyle.THROUGH, "oppositeDirection" : true, "holeDiameter" : 5 * mm, "isTappedThrough" : true, "tappedDepth" : 12 * mm, "tapClearance" : 3, "locations" : qUnion([Q0]), "scope" : qUnion([Q1])});
        }
        {
            var Q0;
            Q0=sQuery(id+"F0.wireOp",VERTEX,"E375.end");
            var Q1;
            Q1=makeQuery(id+"F1.opExtrude","SWEPT_BODY",BODY,{"disambiguationData":[OSD([sQuery(id+"F0.wireOp",EDGE,"E127"),sQuery(id+"F0.wireOp",EDGE,"E133"),sQuery(id+"F0.wireOp",EDGE,"E137"),sQuery(id+"F0.wireOp",EDGE,"E139"),sQuery(id+"F0.wireOp",EDGE,"E233"),sQuery(id+"F0.wireOp",EDGE,"E315"),sQuery(id+"F0.wireOp",EDGE,"E328"),sQuery(id+"F0.wireOp",EDGE,"E331"),sQuery(id+"F0.wireOp",EDGE,"E332"),sQuery(id+"F0.wireOp",EDGE,"E355"),sQuery(id+"F0.wireOp",EDGE,"E357"),sQuery(id+"F0.wireOp",EDGE,"E376"),sQuery(id+"F0.wireOp",EDGE,"E377"),sQuery(id+"F0.wireOp",EDGE,"E543"),sQuery(id+"F0.wireOp",EDGE,"E544"),sQuery(id+"F0.wireOp",EDGE,"E546"),sQuery(id+"F0.wireOp",EDGE,"E553"),sQuery(id+"F0.wireOp",EDGE,"E554"),sQuery(id+"F0.wireOp",EDGE,"E556"),sQuery(id+"F0.wireOp",EDGE,"E557"),sQuery(id+"F0.wireOp",EDGE,"E722")])]});
            hole(context, id + "F3", {"style" : HoleStyle.SIMPLE, "endStyle" : HoleEndStyle.THROUGH, "oppositeDirection" : true, "holeDiameter" : 5 * mm, "isTappedThrough" : true, "tappedDepth" : 12 * mm, "tapClearance" : 3, "locations" : qUnion([Q0]), "scope" : qUnion([Q1])});
        }
        {
            var Q0;
            {var subQ0=sQuery(id+"F0.wireOp",EDGE,"E136");var subQ1=sQuery(id+"F0.wireOp",EDGE,"E124");var subQ2=makeQuery(id+"F0.imprint","INTERSECT",VERTEX,{"derivedFrom":[subQ1,subQ0]});Q0=makeQuery(id+"F0.imprint","IMPRINT",FACE,{"disambiguationData":[TD([[makeQuery(id+"F0.imprint","IMPRINT",EDGE,{"disambiguationData":[TD([[subQ2,-1.0]])],"derivedFrom":subQ1}),1.0]])]});}
            var Q1;
            {var subQ0=sQuery(id+"F0.wireOp",EDGE,"E722");var subQ1=sQuery(id+"F0.wireOp",EDGE,"E124");var subQ2=makeQuery(id+"F0.imprint","INTERSECT",VERTEX,{"disambiguationData":[OD(0.0)],"derivedFrom":[subQ1,subQ0]});Q1=makeQuery(id+"F0.imprint","IMPRINT",FACE,{"disambiguationData":[TD([[makeQuery(id+"F0.imprint","IMPRINT",EDGE,{"disambiguationData":[TD([[subQ2,-1.0]])],"derivedFrom":subQ1}),1.0]])]});}
            var Q2;
            {var subQ5=sQuery(id+"F0.wireOp",EDGE,"E241");Q2=makeQuery(id+"F0.imprint","IMPRINT",FACE,{"disambiguationData":[TD([[makeQuery(id+"F0.imprint","IMPRINT",EDGE,{"derivedFrom":subQ5}),-1.0]])]});}
            var Q3;
            {var subQ4=sQuery(id+"F0.wireOp",EDGE,"E135");Q3=makeQuery(id+"F0.imprint","IMPRINT",FACE,{"disambiguationData":[TD([[makeQuery(id+"F0.imprint","IMPRINT",EDGE,{"derivedFrom":subQ4}),1.0]])]});}
            extrude(context, id + "F4", {"entities" : qUnion([Q0, Q1, Q2, Q3]), "operationType" : NewBodyOperationType.ADD, "depth" : 1.5 * mm});
        }
        {
            var Q0;
            Q0=makeQuery(id+"F1.opExtrude","CAP_FACE",FACE,{"disambiguationData":[OSD([sQuery(id+"F0.wireOp",EDGE,"E127"),sQuery(id+"F0.wireOp",EDGE,"E133"),sQuery(id+"F0.wireOp",EDGE,"E137"),sQuery(id+"F0.wireOp",EDGE,"E139"),sQuery(id+"F0.wireOp",EDGE,"E233"),sQuery(id+"F0.wireOp",EDGE,"E315"),sQuery(id+"F0.wireOp",EDGE,"E328"),sQuery(id+"F0.wireOp",EDGE,"E331"),sQuery(id+"F0.wireOp",EDGE,"E332"),sQuery(id+"F0.wireOp",EDGE,"E355"),sQuery(id+"F0.wireOp",EDGE,"E357"),sQuery(id+"F0.wireOp",EDGE,"E376"),sQuery(id+"F0.wireOp",EDGE,"E377"),sQuery(id+"F0.wireOp",EDGE,"E543"),sQuery(id+"F0.wireOp",EDGE,"E544"),sQuery(id+"F0.wireOp",EDGE,"E546"),sQuery(id+"F0.wireOp",EDGE,"E553"),sQuery(id+"F0.wireOp",EDGE,"E554"),sQuery(id+"F0.wireOp",EDGE,"E556"),sQuery(id+"F0.wireOp",EDGE,"E557"),sQuery(id+"F0.wireOp",EDGE,"E722")])],"isStart":false});
            var sketch = newSketch(context, id + "F5", { "sketchPlane" : qUnion([Q0])});
            skArc(sketch, "E725", {"start": v(-190.62, 25.3) * mm, "mid": v(-127.03, 59.03) * mm, "end": v(-197.59, 44.78) * mm});
            skArc(sketch, "E726", {"start": v(-124.96, 48.78) * mm, "mid": v(-173.52, 81.03) * mm, "end": v(-190.62, 25.3) * mm});
            skArc(sketch, "E727", {"start": v(-190.62, 25.3) * mm, "mid": v(-155.07, 29.45) * mm, "end": v(-124.96, 48.78) * mm});
            skSolve(sketch);
        }
        {
            var Q0;
            Q0=makeQuery(id+"F5.imprint","IMPRINT",FACE,{"disambiguationData":[TD([[makeQuery(id+"F5.imprint","IMPRINT",EDGE,{"derivedFrom":sQuery(id+"F5.wireOp",EDGE,"E727")}),1.0]])]});
            extrude(context, id + "F6", {"entities" : qUnion([Q0]), "oppositeDirection" : true, "depth" : 1.5 * mm});
        }
    });
